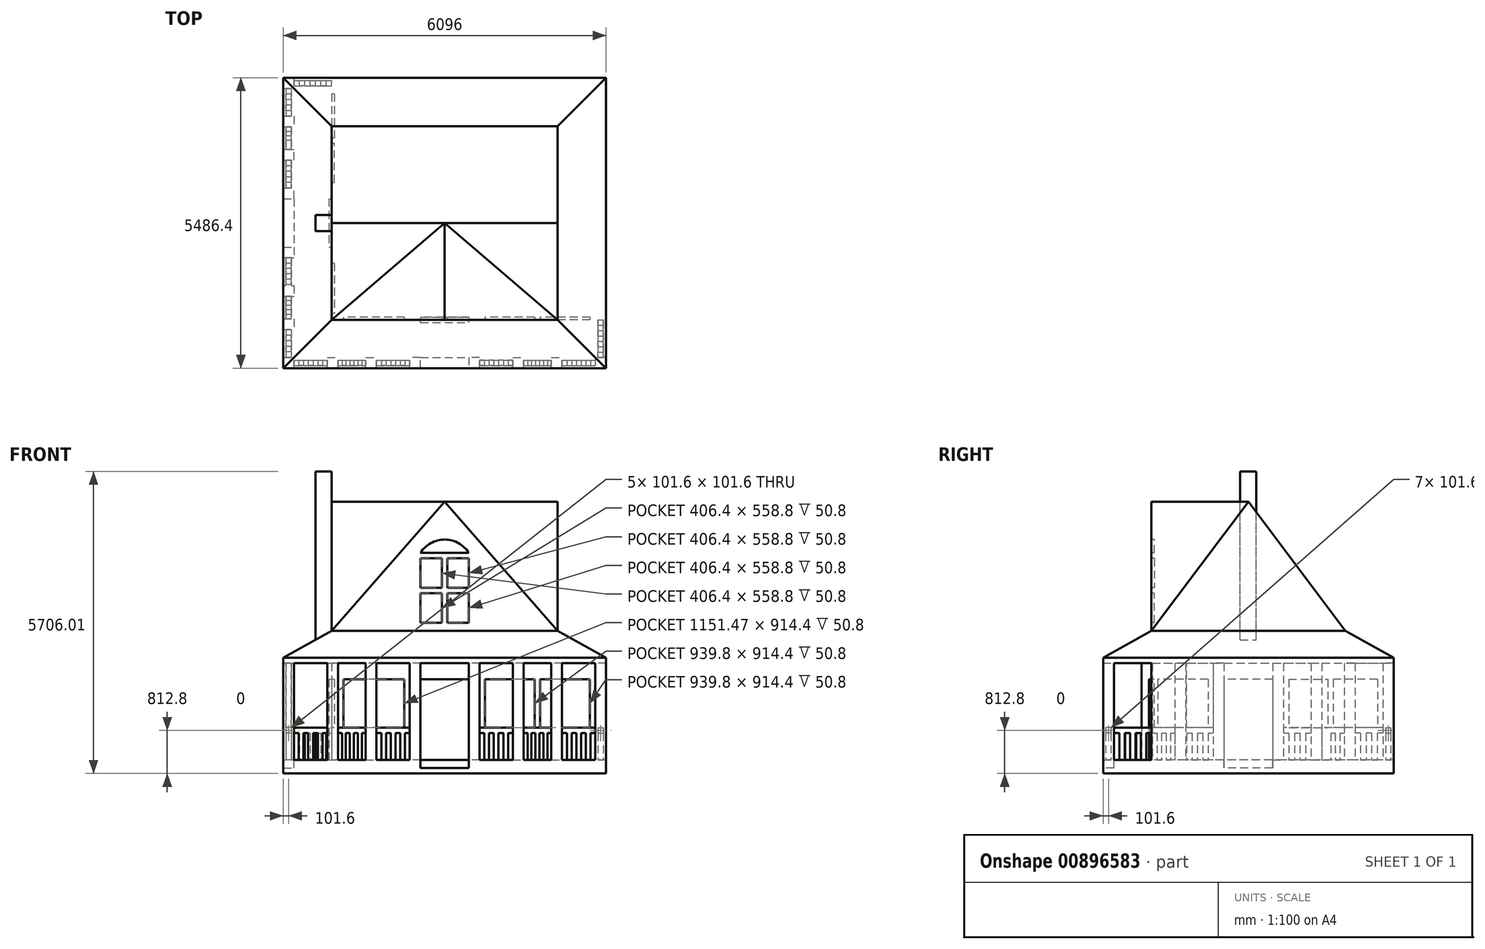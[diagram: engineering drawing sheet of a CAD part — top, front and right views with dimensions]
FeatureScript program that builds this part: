
annotation { "Feature Type Name" : "Feature", "Feature Type Description" : "" }
export const myFeature = defineFeature(function(context is Context, id is Id, definition is map)
    precondition{}
    {
        {
            var Q0;
            Q0=qCreatedBy(makeId("Top.planeOp"),FACE);
            var sketch = newSketch(context, id + "F0", { "sketchPlane" : qUnion([Q0])});
            skLineSegment(sketch, "E0.bottom", {"start": v(-3048, 2743.2) * mm, "end": v(3048, 2743.2) * mm});
            skLineSegment(sketch, "E0.top", {"start": v(-3048, -2743.2) * mm, "end": v(3048, -2743.2) * mm});
            skLineSegment(sketch, "E0.left", {"start": v(-3048, 2743.2) * mm, "end": v(-3048, -2743.2) * mm});
            skLineSegment(sketch, "E0.right", {"start": v(3048, 2743.2) * mm, "end": v(3048, -2743.2) * mm});
            skSolve(sketch);
        }
        {
            var Q0;
            Q0 = qSketchRegion(id + "F0", true);
            extrude(context, id + "F1", {"entities" : qUnion([Q0]), "depth" : 254 * mm, "offsetDistance" : 25.4 * mm});
        }
        {
            var Q0;
            Q0=makeQuery(id+"F1.opExtrude","CAP_FACE",FACE,{"disambiguationData":[OSD([sQuery(id+"F0.wireOp",EDGE,"E0.bottom"),sQuery(id+"F0.wireOp",EDGE,"E0.top"),sQuery(id+"F0.wireOp",EDGE,"E0.left"),sQuery(id+"F0.wireOp",EDGE,"E0.right")])],"isStart":false});
            var sketch = newSketch(context, id + "F2", { "sketchPlane" : qUnion([Q0])});
            skLineSegment(sketch, "E1", {"start": v(-2133.6, 2743.2) * mm, "end": v(-2133.6, -1828.8) * mm, "construction": true});
            skLineSegment(sketch, "E2", {"start": v(-2133.6, -1828.8) * mm, "end": v(3048, -1828.8) * mm, "construction": true});
            skLineSegment(sketch, "E3", {"start": v(0, -2743.2) * mm, "end": v(457.2, -2743.2) * mm, "construction": true});
            skLineSegment(sketch, "E4", {"start": v(0, -2743.2) * mm, "end": v(-457.2, -2743.2) * mm, "construction": true});
            skLineSegment(sketch, "E5", {"start": v(-3048, 0) * mm, "end": v(-3048, 457.2) * mm, "construction": true});
            skLineSegment(sketch, "E6", {"start": v(-3048, 0) * mm, "end": v(-3048, -457.2) * mm, "construction": true});
            skLineSegment(sketch, "E7", {"start": v(3048, -2743.2) * mm, "end": v(3048, -2540) * mm});
            skLineSegment(sketch, "E8", {"start": v(3048, -2540) * mm, "end": v(2844.8, -2540) * mm});
            skLineSegment(sketch, "E9", {"start": v(2844.8, -2540) * mm, "end": v(2844.8, -2743.2) * mm});
            skLineSegment(sketch, "E10", {"start": v(2844.8, -2743.2) * mm, "end": v(3048, -2743.2) * mm});
            skLineSegment(sketch, "E11", {"start": v(457.2, -2743.2) * mm, "end": v(660.4, -2743.2) * mm});
            skLineSegment(sketch, "E12", {"start": v(660.4, -2743.2) * mm, "end": v(660.4, -2540) * mm});
            skLineSegment(sketch, "E13", {"start": v(660.4, -2540) * mm, "end": v(457.2, -2540) * mm});
            skLineSegment(sketch, "E14", {"start": v(457.2, -2540) * mm, "end": v(457.2, -2743.2) * mm});
            skLineSegment(sketch, "E15", {"start": v(660.4, -2641.6) * mm, "end": v(1388.53, -2641.6) * mm, "construction": true});
            skLineSegment(sketch, "E16", {"start": v(1388.53, -2641.6) * mm, "end": v(2116.67, -2641.6) * mm, "construction": true});
            skLineSegment(sketch, "E17", {"start": v(2116.67, -2641.6) * mm, "end": v(2844.8, -2641.6) * mm, "construction": true});
            skLineSegment(sketch, "E18.bottom", {"start": v(1286.93, -2743.2) * mm, "end": v(1490.13, -2743.2) * mm});
            skLineSegment(sketch, "E18.top", {"start": v(1286.93, -2540) * mm, "end": v(1490.13, -2540) * mm});
            skLineSegment(sketch, "E18.left", {"start": v(1286.93, -2743.2) * mm, "end": v(1286.93, -2540) * mm});
            skLineSegment(sketch, "E18.right", {"start": v(1490.13, -2743.2) * mm, "end": v(1490.13, -2540) * mm});
            skLineSegment(sketch, "E19.bottom", {"start": v(2015.07, -2743.2) * mm, "end": v(2218.27, -2743.2) * mm});
            skLineSegment(sketch, "E19.top", {"start": v(2015.07, -2540) * mm, "end": v(2218.27, -2540) * mm});
            skLineSegment(sketch, "E19.left", {"start": v(2015.07, -2743.2) * mm, "end": v(2015.07, -2540) * mm});
            skLineSegment(sketch, "E19.right", {"start": v(2218.27, -2743.2) * mm, "end": v(2218.27, -2540) * mm});
            skLineSegment(sketch, "E20", {"start": v(660.4, -2692.4) * mm, "end": v(1286.93, -2692.4) * mm});
            skLineSegment(sketch, "E21", {"start": v(1490.13, -2692.4) * mm, "end": v(2015.07, -2692.4) * mm});
            skLineSegment(sketch, "E22", {"start": v(2218.27, -2692.4) * mm, "end": v(2844.8, -2692.4) * mm});
            skLineSegment(sketch, "E23", {"start": v(660.4, -2590.8) * mm, "end": v(1286.93, -2590.8) * mm});
            skLineSegment(sketch, "E24", {"start": v(1490.13, -2590.8) * mm, "end": v(2015.07, -2590.8) * mm});
            skLineSegment(sketch, "E25", {"start": v(2218.27, -2590.8) * mm, "end": v(2844.8, -2590.8) * mm});
            skLineSegment(sketch, "E26.bottom", {"start": v(-457.2, -2743.2) * mm, "end": v(-660.4, -2743.2) * mm});
            skLineSegment(sketch, "E26.top", {"start": v(-457.2, -2540) * mm, "end": v(-660.4, -2540) * mm});
            skLineSegment(sketch, "E26.left", {"start": v(-457.2, -2743.2) * mm, "end": v(-457.2, -2540) * mm});
            skLineSegment(sketch, "E26.right", {"start": v(-660.4, -2743.2) * mm, "end": v(-660.4, -2540) * mm});
            skLineSegment(sketch, "E27.bottom", {"start": v(-3048, -2743.2) * mm, "end": v(-2844.8, -2743.2) * mm});
            skLineSegment(sketch, "E27.top", {"start": v(-3048, -2540) * mm, "end": v(-2844.8, -2540) * mm});
            skLineSegment(sketch, "E27.left", {"start": v(-3048, -2743.2) * mm, "end": v(-3048, -2540) * mm});
            skLineSegment(sketch, "E27.right", {"start": v(-2844.8, -2743.2) * mm, "end": v(-2844.8, -2540) * mm});
            skLineSegment(sketch, "E28", {"start": v(-2844.8, -2641.6) * mm, "end": v(-2116.67, -2641.6) * mm, "construction": true});
            skLineSegment(sketch, "E29", {"start": v(-2116.67, -2641.6) * mm, "end": v(-1388.53, -2641.6) * mm, "construction": true});
            skLineSegment(sketch, "E30", {"start": v(-1388.53, -2641.6) * mm, "end": v(-660.4, -2641.6) * mm, "construction": true});
            skLineSegment(sketch, "E31.bottom", {"start": v(-2218.27, -2743.2) * mm, "end": v(-2015.07, -2743.2) * mm});
            skLineSegment(sketch, "E31.top", {"start": v(-2218.27, -2540) * mm, "end": v(-2015.07, -2540) * mm});
            skLineSegment(sketch, "E31.left", {"start": v(-2218.27, -2743.2) * mm, "end": v(-2218.27, -2540) * mm});
            skLineSegment(sketch, "E31.right", {"start": v(-2015.07, -2743.2) * mm, "end": v(-2015.07, -2540) * mm});
            skLineSegment(sketch, "E32.bottom", {"start": v(-1490.13, -2743.2) * mm, "end": v(-1286.93, -2743.2) * mm});
            skLineSegment(sketch, "E32.top", {"start": v(-1490.13, -2540) * mm, "end": v(-1286.93, -2540) * mm});
            skLineSegment(sketch, "E32.left", {"start": v(-1490.13, -2743.2) * mm, "end": v(-1490.13, -2540) * mm});
            skLineSegment(sketch, "E32.right", {"start": v(-1286.93, -2743.2) * mm, "end": v(-1286.93, -2540) * mm});
            skLineSegment(sketch, "E33", {"start": v(-457.2, -2692.4) * mm, "end": v(-660.4, -2692.4) * mm, "construction": true});
            skLineSegment(sketch, "E34", {"start": v(-660.4, -2692.4) * mm, "end": v(-1286.93, -2692.4) * mm});
            skLineSegment(sketch, "E35", {"start": v(-1286.93, -2692.4) * mm, "end": v(-1490.13, -2692.4) * mm, "construction": true});
            skLineSegment(sketch, "E36", {"start": v(-1490.13, -2692.4) * mm, "end": v(-2015.07, -2692.4) * mm});
            skLineSegment(sketch, "E37", {"start": v(-2015.07, -2692.4) * mm, "end": v(-2218.27, -2692.4) * mm, "construction": true});
            skLineSegment(sketch, "E38", {"start": v(-2218.27, -2692.4) * mm, "end": v(-2844.8, -2692.4) * mm});
            skLineSegment(sketch, "E39", {"start": v(-2844.8, -2590.8) * mm, "end": v(-2218.27, -2590.8) * mm});
            skLineSegment(sketch, "E40", {"start": v(-2218.27, -2590.8) * mm, "end": v(-2015.07, -2590.8) * mm, "construction": true});
            skLineSegment(sketch, "E41", {"start": v(-2015.07, -2590.8) * mm, "end": v(-1490.13, -2590.8) * mm});
            skLineSegment(sketch, "E42", {"start": v(-1490.13, -2590.8) * mm, "end": v(-1286.93, -2590.8) * mm, "construction": true});
            skLineSegment(sketch, "E43", {"start": v(-1286.93, -2590.8) * mm, "end": v(-660.4, -2590.8) * mm});
            skLineSegment(sketch, "E44", {"start": v(-660.4, -2590.8) * mm, "end": v(-457.2, -2590.8) * mm, "construction": true});
            skLineSegment(sketch, "E45", {"start": v(-3048, -457.2) * mm, "end": v(-2844.8, -457.2) * mm});
            skLineSegment(sketch, "E46", {"start": v(-2844.8, -457.2) * mm, "end": v(-2844.8, -660.4) * mm});
            skLineSegment(sketch, "E47", {"start": v(-2844.8, -660.4) * mm, "end": v(-3048, -660.4) * mm});
            skLineSegment(sketch, "E48", {"start": v(-3048, -660.4) * mm, "end": v(-3048, -457.2) * mm});
            skLineSegment(sketch, "E49", {"start": v(-2946.4, -660.4) * mm, "end": v(-2946.4, -1286.93) * mm, "construction": true});
            skLineSegment(sketch, "E50", {"start": v(-2946.4, -1286.93) * mm, "end": v(-2946.4, -1913.47) * mm, "construction": true});
            skLineSegment(sketch, "E51", {"start": v(-2946.4, -1913.47) * mm, "end": v(-2946.4, -2540) * mm, "construction": true});
            skLineSegment(sketch, "E52.bottom", {"start": v(-3048, -1185.33) * mm, "end": v(-2844.8, -1185.33) * mm});
            skLineSegment(sketch, "E52.top", {"start": v(-3048, -1388.53) * mm, "end": v(-2844.8, -1388.53) * mm});
            skLineSegment(sketch, "E52.left", {"start": v(-3048, -1185.33) * mm, "end": v(-3048, -1388.53) * mm});
            skLineSegment(sketch, "E52.right", {"start": v(-2844.8, -1185.33) * mm, "end": v(-2844.8, -1388.53) * mm});
            skLineSegment(sketch, "E53.bottom", {"start": v(-3048, -1811.87) * mm, "end": v(-2844.8, -1811.87) * mm});
            skLineSegment(sketch, "E53.top", {"start": v(-3048, -2015.07) * mm, "end": v(-2844.8, -2015.07) * mm});
            skLineSegment(sketch, "E53.left", {"start": v(-3048, -1811.87) * mm, "end": v(-3048, -2015.07) * mm});
            skLineSegment(sketch, "E53.right", {"start": v(-2844.8, -1811.87) * mm, "end": v(-2844.8, -2015.07) * mm});
            skLineSegment(sketch, "E54.bottom", {"start": v(-3048, 457.2) * mm, "end": v(-2844.8, 457.2) * mm});
            skLineSegment(sketch, "E54.top", {"start": v(-3048, 660.4) * mm, "end": v(-2844.8, 660.4) * mm});
            skLineSegment(sketch, "E54.left", {"start": v(-3048, 457.2) * mm, "end": v(-3048, 660.4) * mm});
            skLineSegment(sketch, "E54.right", {"start": v(-2844.8, 457.2) * mm, "end": v(-2844.8, 660.4) * mm});
            skLineSegment(sketch, "E55.bottom", {"start": v(-3048, 2743.2) * mm, "end": v(-2844.8, 2743.2) * mm});
            skLineSegment(sketch, "E55.top", {"start": v(-3048, 2540) * mm, "end": v(-2844.8, 2540) * mm});
            skLineSegment(sketch, "E55.left", {"start": v(-3048, 2743.2) * mm, "end": v(-3048, 2540) * mm});
            skLineSegment(sketch, "E55.right", {"start": v(-2844.8, 2743.2) * mm, "end": v(-2844.8, 2540) * mm});
            skLineSegment(sketch, "E56", {"start": v(-2946.4, 2540) * mm, "end": v(-2946.4, 1913.47) * mm, "construction": true});
            skLineSegment(sketch, "E57", {"start": v(-2946.4, 1913.47) * mm, "end": v(-2946.4, 1286.93) * mm, "construction": true});
            skLineSegment(sketch, "E58", {"start": v(-2946.4, 1286.93) * mm, "end": v(-2946.4, 660.4) * mm, "construction": true});
            skLineSegment(sketch, "E59", {"start": v(2997.2, -2540) * mm, "end": v(2997.2, -1828.8) * mm});
            skLineSegment(sketch, "E60", {"start": v(2997.2, -1828.8) * mm, "end": v(2895.6, -1828.8) * mm});
            skLineSegment(sketch, "E61", {"start": v(2895.6, -1828.8) * mm, "end": v(2895.6, -2540) * mm});
            skLineSegment(sketch, "E62", {"start": v(-2844.8, 2692.4) * mm, "end": v(-2133.6, 2692.4) * mm});
            skLineSegment(sketch, "E63", {"start": v(-2133.6, 2692.4) * mm, "end": v(-2133.6, 2590.8) * mm});
            skLineSegment(sketch, "E64", {"start": v(-2133.6, 2590.8) * mm, "end": v(-2844.8, 2590.8) * mm});
            skLineSegment(sketch, "E65.bottom", {"start": v(-3048, 2015.07) * mm, "end": v(-2844.8, 2015.07) * mm});
            skLineSegment(sketch, "E65.top", {"start": v(-3048, 1811.87) * mm, "end": v(-2844.8, 1811.87) * mm});
            skLineSegment(sketch, "E65.left", {"start": v(-3048, 2015.07) * mm, "end": v(-3048, 1811.87) * mm});
            skLineSegment(sketch, "E65.right", {"start": v(-2844.8, 2015.07) * mm, "end": v(-2844.8, 1811.87) * mm});
            skLineSegment(sketch, "E66.bottom", {"start": v(-3048, 1185.33) * mm, "end": v(-2844.8, 1185.33) * mm});
            skLineSegment(sketch, "E66.top", {"start": v(-3048, 1388.53) * mm, "end": v(-2844.8, 1388.53) * mm});
            skLineSegment(sketch, "E66.left", {"start": v(-3048, 1185.33) * mm, "end": v(-3048, 1388.53) * mm});
            skLineSegment(sketch, "E66.right", {"start": v(-2844.8, 1185.33) * mm, "end": v(-2844.8, 1388.53) * mm});
            skLineSegment(sketch, "E67", {"start": v(-2997.2, -2540) * mm, "end": v(-2997.2, -2015.07) * mm});
            skLineSegment(sketch, "E68", {"start": v(-2895.6, -2540) * mm, "end": v(-2895.6, -2015.07) * mm});
            skLineSegment(sketch, "E69", {"start": v(-2997.2, -2015.07) * mm, "end": v(-2997.2, -1811.87) * mm, "construction": true});
            skLineSegment(sketch, "E70", {"start": v(-2997.2, -1811.87) * mm, "end": v(-2997.2, -1388.53) * mm});
            skLineSegment(sketch, "E71", {"start": v(-2997.2, -1388.53) * mm, "end": v(-2997.2, -1185.33) * mm, "construction": true});
            skLineSegment(sketch, "E72", {"start": v(-2997.2, -1185.33) * mm, "end": v(-2997.2, -660.4) * mm});
            skLineSegment(sketch, "E73", {"start": v(-2895.6, -2015.07) * mm, "end": v(-2895.6, -1811.87) * mm, "construction": true});
            skLineSegment(sketch, "E74", {"start": v(-2895.6, -1811.87) * mm, "end": v(-2895.6, -1388.53) * mm});
            skLineSegment(sketch, "E75", {"start": v(-2895.6, -1388.53) * mm, "end": v(-2895.6, -1185.33) * mm, "construction": true});
            skLineSegment(sketch, "E76", {"start": v(-2895.6, -1185.33) * mm, "end": v(-2895.6, -660.4) * mm});
            skLineSegment(sketch, "E77", {"start": v(-2997.2, 660.4) * mm, "end": v(-2997.2, 1185.33) * mm});
            skLineSegment(sketch, "E78", {"start": v(-2895.6, 660.4) * mm, "end": v(-2895.6, 1185.33) * mm});
            skLineSegment(sketch, "E79", {"start": v(-2997.2, 1185.33) * mm, "end": v(-2997.2, 1388.53) * mm, "construction": true});
            skLineSegment(sketch, "E80", {"start": v(-2997.2, 1388.53) * mm, "end": v(-2997.2, 1811.87) * mm});
            skLineSegment(sketch, "E81", {"start": v(-2997.2, 1811.87) * mm, "end": v(-2997.2, 2015.07) * mm, "construction": true});
            skLineSegment(sketch, "E82", {"start": v(-2997.2, 2015.07) * mm, "end": v(-2997.2, 2540) * mm});
            skLineSegment(sketch, "E83", {"start": v(-2895.6, 1185.33) * mm, "end": v(-2895.6, 1388.53) * mm, "construction": true});
            skLineSegment(sketch, "E84", {"start": v(-2895.6, 1388.53) * mm, "end": v(-2895.6, 1811.87) * mm});
            skLineSegment(sketch, "E85", {"start": v(-2895.6, 1811.87) * mm, "end": v(-2895.6, 2015.07) * mm, "construction": true});
            skLineSegment(sketch, "E86", {"start": v(-2895.6, 2015.07) * mm, "end": v(-2895.6, 2540) * mm});
            skSolve(sketch);
        }
        {
            var Q0;
            Q0 = qSketchRegion(id + "F2", true);
            extrude(context, id + "F3", {"entities" : qUnion([Q0]), "operationType" : NewBodyOperationType.ADD, "depth" : 1828.8 * mm, "offsetDistance" : 25.4 * mm});
        }
        {
            var Q0;
            Q0=makeQuery(id+"F3.opExtrude","SWEPT_FACE",FACE,{"disambiguationData":[OSD([sQuery(id+"F2.wireOp",EDGE,"E22")])]});
            var sketch = newSketch(context, id + "F4", { "sketchPlane" : qUnion([Q0])});
            skLineSegment(sketch, "E87.0", {"start": v(-2844.8, 863.6) * mm, "end": v(-2218.27, 863.6) * mm});
            skLineSegment(sketch, "E88", {"start": v(2844.8, 863.6) * mm, "end": v(2844.8, 2082.8) * mm});
            skLineSegment(sketch, "E89", {"start": v(2844.8, 2082.8) * mm, "end": v(2218.27, 2082.8) * mm});
            skLineSegment(sketch, "E90", {"start": v(2218.27, 2082.8) * mm, "end": v(2218.27, 863.6) * mm});
            skLineSegment(sketch, "E91.1", {"start": v(1490.13, 2082.8) * mm, "end": v(1490.13, 863.6) * mm});
            skLineSegment(sketch, "E91.2", {"start": v(2015.07, 2082.8) * mm, "end": v(1490.13, 2082.8) * mm});
            skLineSegment(sketch, "E91.3", {"start": v(2015.07, 863.6) * mm, "end": v(2015.07, 2082.8) * mm});
            skLineSegment(sketch, "E92.1", {"start": v(660.4, 2082.8) * mm, "end": v(660.4, 863.6) * mm});
            skLineSegment(sketch, "E92.2", {"start": v(1286.93, 2082.8) * mm, "end": v(660.4, 2082.8) * mm});
            skLineSegment(sketch, "E92.3", {"start": v(1286.93, 863.6) * mm, "end": v(1286.93, 2082.8) * mm});
            skLineSegment(sketch, "E93.1", {"start": v(-1286.93, 2082.8) * mm, "end": v(-1286.93, 863.6) * mm});
            skLineSegment(sketch, "E93.2", {"start": v(-660.4, 2082.8) * mm, "end": v(-1286.93, 2082.8) * mm});
            skLineSegment(sketch, "E93.3", {"start": v(-660.4, 863.6) * mm, "end": v(-660.4, 2082.8) * mm});
            skLineSegment(sketch, "E94.1", {"start": v(-2015.07, 2082.8) * mm, "end": v(-2015.07, 863.6) * mm});
            skLineSegment(sketch, "E94.2", {"start": v(-1490.13, 2082.8) * mm, "end": v(-2015.07, 2082.8) * mm});
            skLineSegment(sketch, "E94.3", {"start": v(-1490.13, 863.6) * mm, "end": v(-1490.13, 2082.8) * mm});
            skLineSegment(sketch, "E95.1", {"start": v(-2844.8, 2082.8) * mm, "end": v(-2844.8, 863.6) * mm});
            skLineSegment(sketch, "E95.2", {"start": v(-2218.27, 2082.8) * mm, "end": v(-2844.8, 2082.8) * mm});
            skLineSegment(sketch, "E95.3", {"start": v(-2218.27, 863.6) * mm, "end": v(-2218.27, 2082.8) * mm});
            skLineSegment(sketch, "E96.trimOffspring", {"start": v(2218.27, 863.6) * mm, "end": v(2844.8, 863.6) * mm});
            skLineSegment(sketch, "E97.trimOffspring", {"start": v(1490.13, 863.6) * mm, "end": v(2015.07, 863.6) * mm});
            skLineSegment(sketch, "E98.trimOffspring", {"start": v(660.4, 863.6) * mm, "end": v(1286.93, 863.6) * mm});
            skLineSegment(sketch, "E99.trimOffspring", {"start": v(-1286.93, 863.6) * mm, "end": v(-660.4, 863.6) * mm});
            skLineSegment(sketch, "E100.trimOffspring", {"start": v(-2015.07, 863.6) * mm, "end": v(-1490.13, 863.6) * mm});
            skLineSegment(sketch, "E101.0", {"start": v(2218.27, 762) * mm, "end": v(2307.77, 762) * mm});
            skLineSegment(sketch, "E102.0", {"start": v(1490.13, 762) * mm, "end": v(1565.12, 762) * mm});
            skLineSegment(sketch, "E103.0", {"start": v(-1286.93, 762) * mm, "end": v(-1197.43, 762) * mm});
            skLineSegment(sketch, "E104.0", {"start": v(-2015.07, 762) * mm, "end": v(-1940.08, 762) * mm});
            skLineSegment(sketch, "E105.0", {"start": v(-2844.8, 762) * mm, "end": v(-2755.3, 762) * mm});
            skLineSegment(sketch, "E106", {"start": v(-2665.8, 762) * mm, "end": v(-2576.29, 762) * mm});
            skLineSegment(sketch, "E107", {"start": v(-2486.78, 762) * mm, "end": v(-2397.28, 762) * mm});
            skLineSegment(sketch, "E108", {"start": v(-2307.77, 762) * mm, "end": v(-2218.27, 762) * mm});
            skLineSegment(sketch, "E109.0", {"start": v(-2844.8, 254) * mm, "end": v(-2755.3, 254) * mm});
            skLineSegment(sketch, "E110.0", {"start": v(-2015.07, 254) * mm, "end": v(-1490.13, 254) * mm});
            skLineSegment(sketch, "E111.0", {"start": v(-1286.93, 254) * mm, "end": v(-660.4, 254) * mm});
            skLineSegment(sketch, "E112.0", {"start": v(660.4, 254) * mm, "end": v(1286.93, 254) * mm});
            skLineSegment(sketch, "E113.0", {"start": v(1490.13, 254) * mm, "end": v(2015.07, 254) * mm});
            skLineSegment(sketch, "E114.0", {"start": v(2218.27, 254) * mm, "end": v(2844.8, 254) * mm});
            skLineSegment(sketch, "E115", {"start": v(-2755.3, 762) * mm, "end": v(-2755.3, 254) * mm});
            skLineSegment(sketch, "E116", {"start": v(-2665.8, 762) * mm, "end": v(-2665.8, 254) * mm});
            skLineSegment(sketch, "E117", {"start": v(-2576.29, 762) * mm, "end": v(-2576.29, 254) * mm});
            skLineSegment(sketch, "E118", {"start": v(-2486.78, 762) * mm, "end": v(-2486.78, 254) * mm});
            skLineSegment(sketch, "E119", {"start": v(-2397.28, 762) * mm, "end": v(-2397.28, 254) * mm});
            skLineSegment(sketch, "E120", {"start": v(-2307.77, 762) * mm, "end": v(-2307.77, 254) * mm});
            skLineSegment(sketch, "E121.trimOffspring", {"start": v(-2307.77, 254) * mm, "end": v(-2218.27, 254) * mm});
            skLineSegment(sketch, "E122.trimOffspring", {"start": v(-2486.78, 254) * mm, "end": v(-2397.28, 254) * mm});
            skLineSegment(sketch, "E123.trimOffspring", {"start": v(-2665.8, 254) * mm, "end": v(-2576.29, 254) * mm});
            skLineSegment(sketch, "E124", {"start": v(-2844.8, 762) * mm, "end": v(-2844.8, 254) * mm});
            skLineSegment(sketch, "E125", {"start": v(-2755.3, 254) * mm, "end": v(-2844.8, 254) * mm});
            skLineSegment(sketch, "E126", {"start": v(-2218.27, 762) * mm, "end": v(-2218.27, 254) * mm});
            skLineSegment(sketch, "E127", {"start": v(-1865.09, 762) * mm, "end": v(-1790.1, 762) * mm});
            skLineSegment(sketch, "E128", {"start": v(-1715.1, 762) * mm, "end": v(-1640.11, 762) * mm});
            skLineSegment(sketch, "E129", {"start": v(-1565.12, 762) * mm, "end": v(-1490.13, 762) * mm});
            skLineSegment(sketch, "E130", {"start": v(-1107.92, 762) * mm, "end": v(-1018.42, 762) * mm});
            skLineSegment(sketch, "E131", {"start": v(-928.91, 762) * mm, "end": v(-839.4, 762) * mm});
            skLineSegment(sketch, "E132", {"start": v(-749.9, 762) * mm, "end": v(-660.4, 762) * mm});
            skLineSegment(sketch, "E133", {"start": v(1640.11, 762) * mm, "end": v(1715.1, 762) * mm});
            skLineSegment(sketch, "E134", {"start": v(1790.1, 762) * mm, "end": v(1865.09, 762) * mm});
            skLineSegment(sketch, "E135", {"start": v(1940.08, 762) * mm, "end": v(2015.07, 762) * mm});
            skLineSegment(sketch, "E136", {"start": v(2397.28, 762) * mm, "end": v(2486.78, 762) * mm});
            skLineSegment(sketch, "E137", {"start": v(2576.29, 762) * mm, "end": v(2665.8, 762) * mm});
            skLineSegment(sketch, "E138", {"start": v(2755.3, 762) * mm, "end": v(2844.8, 762) * mm});
            skLineSegment(sketch, "E139", {"start": v(1286.93, 863.6) * mm, "end": v(1286.93, 762) * mm, "construction": true});
            skLineSegment(sketch, "E140", {"start": v(1286.93, 762) * mm, "end": v(1197.43, 762) * mm});
            skLineSegment(sketch, "E141", {"start": v(1107.92, 762) * mm, "end": v(1018.42, 762) * mm});
            skLineSegment(sketch, "E142", {"start": v(928.91, 762) * mm, "end": v(839.4, 762) * mm});
            skLineSegment(sketch, "E143", {"start": v(749.9, 762) * mm, "end": v(660.4, 762) * mm});
            skLineSegment(sketch, "E144", {"start": v(2844.8, 762) * mm, "end": v(2844.8, 254) * mm});
            skLineSegment(sketch, "E145", {"start": v(2755.3, 762) * mm, "end": v(2755.3, 254) * mm});
            skLineSegment(sketch, "E146", {"start": v(2755.3, 254) * mm, "end": v(2844.8, 254) * mm});
            skLineSegment(sketch, "E147", {"start": v(2665.8, 762) * mm, "end": v(2665.8, 254) * mm});
            skLineSegment(sketch, "E148", {"start": v(2576.29, 762) * mm, "end": v(2576.29, 254) * mm});
            skLineSegment(sketch, "E149", {"start": v(2576.29, 254) * mm, "end": v(2665.8, 254) * mm});
            skLineSegment(sketch, "E150", {"start": v(2486.78, 762) * mm, "end": v(2486.78, 254) * mm});
            skLineSegment(sketch, "E151", {"start": v(2397.28, 762) * mm, "end": v(2397.28, 254) * mm});
            skLineSegment(sketch, "E152", {"start": v(2397.28, 254) * mm, "end": v(2486.78, 254) * mm});
            skLineSegment(sketch, "E153", {"start": v(2307.77, 762) * mm, "end": v(2307.77, 254) * mm});
            skLineSegment(sketch, "E154", {"start": v(2307.77, 254) * mm, "end": v(2218.27, 254) * mm});
            skLineSegment(sketch, "E155", {"start": v(2218.27, 762) * mm, "end": v(2218.27, 254) * mm});
            skLineSegment(sketch, "E156.top", {"start": v(1940.08, 254) * mm, "end": v(2015.07, 254) * mm});
            skLineSegment(sketch, "E156.left", {"start": v(1940.08, 762) * mm, "end": v(1940.08, 254) * mm});
            skLineSegment(sketch, "E156.right", {"start": v(2015.07, 762) * mm, "end": v(2015.07, 254) * mm});
            skLineSegment(sketch, "E157", {"start": v(1865.09, 762) * mm, "end": v(1865.09, 254) * mm});
            skLineSegment(sketch, "E158", {"start": v(1790.1, 762) * mm, "end": v(1790.1, 254) * mm});
            skLineSegment(sketch, "E159", {"start": v(1790.1, 254) * mm, "end": v(1865.09, 254) * mm});
            skLineSegment(sketch, "E160", {"start": v(1715.1, 762) * mm, "end": v(1715.1, 254) * mm});
            skLineSegment(sketch, "E161", {"start": v(1640.11, 762) * mm, "end": v(1640.11, 254) * mm});
            skLineSegment(sketch, "E162", {"start": v(1640.11, 254) * mm, "end": v(1715.1, 254) * mm});
            skLineSegment(sketch, "E163", {"start": v(1565.12, 762) * mm, "end": v(1565.12, 254) * mm});
            skLineSegment(sketch, "E164", {"start": v(1565.12, 254) * mm, "end": v(1490.13, 254) * mm});
            skLineSegment(sketch, "E165", {"start": v(1490.13, 762) * mm, "end": v(1490.13, 254) * mm});
            skLineSegment(sketch, "E166", {"start": v(1197.43, 762) * mm, "end": v(1197.43, 254) * mm});
            skLineSegment(sketch, "E167", {"start": v(1286.93, 762) * mm, "end": v(1286.93, 254) * mm});
            skLineSegment(sketch, "E168", {"start": v(1197.43, 254) * mm, "end": v(1286.93, 254) * mm});
            skLineSegment(sketch, "E169", {"start": v(1107.92, 762) * mm, "end": v(1107.92, 254) * mm});
            skLineSegment(sketch, "E170", {"start": v(1018.42, 762) * mm, "end": v(1018.42, 254) * mm});
            skLineSegment(sketch, "E171", {"start": v(1018.42, 254) * mm, "end": v(1107.92, 254) * mm});
            skLineSegment(sketch, "E172", {"start": v(928.91, 762) * mm, "end": v(928.91, 254) * mm});
            skLineSegment(sketch, "E173", {"start": v(839.4, 762) * mm, "end": v(839.4, 254) * mm});
            skLineSegment(sketch, "E174", {"start": v(839.4, 254) * mm, "end": v(928.91, 254) * mm});
            skLineSegment(sketch, "E175", {"start": v(749.9, 762) * mm, "end": v(749.9, 254) * mm});
            skLineSegment(sketch, "E176", {"start": v(749.9, 254) * mm, "end": v(660.4, 254) * mm});
            skLineSegment(sketch, "E177", {"start": v(660.4, 762) * mm, "end": v(660.4, 254) * mm});
            skLineSegment(sketch, "E178.bottom", {"start": v(-1197.43, 762) * mm, "end": v(-1286.93, 762) * mm});
            skLineSegment(sketch, "E178.top", {"start": v(-1197.43, 254) * mm, "end": v(-1286.93, 254) * mm});
            skLineSegment(sketch, "E178.left", {"start": v(-1197.43, 762) * mm, "end": v(-1197.43, 254) * mm});
            skLineSegment(sketch, "E178.right", {"start": v(-1286.93, 762) * mm, "end": v(-1286.93, 254) * mm});
            skLineSegment(sketch, "E179.top", {"start": v(-749.9, 254) * mm, "end": v(-660.4, 254) * mm});
            skLineSegment(sketch, "E179.left", {"start": v(-749.9, 762) * mm, "end": v(-749.9, 254) * mm});
            skLineSegment(sketch, "E179.right", {"start": v(-660.4, 762) * mm, "end": v(-660.4, 254) * mm});
            skLineSegment(sketch, "E180.bottom", {"start": v(-1940.08, 762) * mm, "end": v(-2015.07, 762) * mm});
            skLineSegment(sketch, "E180.top", {"start": v(-1940.08, 254) * mm, "end": v(-2015.07, 254) * mm});
            skLineSegment(sketch, "E180.left", {"start": v(-1940.08, 762) * mm, "end": v(-1940.08, 254) * mm});
            skLineSegment(sketch, "E180.right", {"start": v(-2015.07, 762) * mm, "end": v(-2015.07, 254) * mm});
            skLineSegment(sketch, "E181.top", {"start": v(-1565.12, 254) * mm, "end": v(-1490.13, 254) * mm});
            skLineSegment(sketch, "E181.left", {"start": v(-1565.12, 762) * mm, "end": v(-1565.12, 254) * mm});
            skLineSegment(sketch, "E181.right", {"start": v(-1490.13, 762) * mm, "end": v(-1490.13, 254) * mm});
            skLineSegment(sketch, "E182", {"start": v(-1865.09, 762) * mm, "end": v(-1865.09, 254) * mm});
            skLineSegment(sketch, "E183", {"start": v(-1790.1, 762) * mm, "end": v(-1790.1, 254) * mm});
            skLineSegment(sketch, "E184", {"start": v(-1715.1, 762) * mm, "end": v(-1715.1, 254) * mm});
            skLineSegment(sketch, "E185", {"start": v(-1640.11, 762) * mm, "end": v(-1640.11, 254) * mm});
            skLineSegment(sketch, "E186", {"start": v(-1640.11, 254) * mm, "end": v(-1715.1, 254) * mm});
            skLineSegment(sketch, "E187", {"start": v(-1790.1, 254) * mm, "end": v(-1865.09, 254) * mm});
            skLineSegment(sketch, "E188", {"start": v(-1107.92, 762) * mm, "end": v(-1107.92, 254) * mm});
            skLineSegment(sketch, "E189", {"start": v(-1018.42, 762) * mm, "end": v(-1018.42, 254) * mm});
            skLineSegment(sketch, "E190", {"start": v(-928.91, 762) * mm, "end": v(-928.91, 254) * mm});
            skLineSegment(sketch, "E191", {"start": v(-839.4, 762) * mm, "end": v(-839.4, 254) * mm});
            skLineSegment(sketch, "E192", {"start": v(-839.4, 254) * mm, "end": v(-928.91, 254) * mm});
            skLineSegment(sketch, "E193", {"start": v(-1018.42, 254) * mm, "end": v(-1107.92, 254) * mm});
            skSolve(sketch);
        }
        {
            var Q0;
            Q0 = qSketchRegion(id + "F4", true);
            extrude(context, id + "F5", {"entities" : qUnion([Q0]), "operationType" : NewBodyOperationType.REMOVE, "oppositeDirection" : true, "depth" : 101.6 * mm, "offsetDistance" : 25.4 * mm});
        }
        {
            var Q0;
            Q0=makeQuery(id+"F3.opExtrude","SWEPT_FACE",FACE,{"disambiguationData":[OSD([sQuery(id+"F2.wireOp",EDGE,"E67")])]});
            var sketch = newSketch(context, id + "F6", { "sketchPlane" : qUnion([Q0])});
            skLineSegment(sketch, "E194.0", {"start": v(2015.07, 863.6) * mm, "end": v(2540, 863.6) * mm});
            skLineSegment(sketch, "E195.0", {"start": v(1388.53, 863.6) * mm, "end": v(1811.87, 863.6) * mm});
            skLineSegment(sketch, "E196.0", {"start": v(654.9, 863.6) * mm, "end": v(1163.3, 863.6) * mm});
            skLineSegment(sketch, "E197.0", {"start": v(-1185.33, 863.6) * mm, "end": v(-660.4, 863.6) * mm});
            skLineSegment(sketch, "E198.0", {"start": v(-1811.87, 863.6) * mm, "end": v(-1388.53, 863.6) * mm});
            skLineSegment(sketch, "E199.0", {"start": v(-2540, 863.6) * mm, "end": v(-2015.07, 863.6) * mm});
            skLineSegment(sketch, "E200", {"start": v(-2540, 863.6) * mm, "end": v(-2540, 2082.8) * mm});
            skLineSegment(sketch, "E201", {"start": v(-2540, 2082.8) * mm, "end": v(-2015.07, 2082.8) * mm});
            skLineSegment(sketch, "E202", {"start": v(2540, 2082.8) * mm, "end": v(2540, 863.6) * mm});
            skLineSegment(sketch, "E203", {"start": v(2015.07, 863.6) * mm, "end": v(2015.07, 2082.8) * mm});
            skLineSegment(sketch, "E204", {"start": v(1811.87, 863.6) * mm, "end": v(1811.87, 2082.8) * mm});
            skLineSegment(sketch, "E205", {"start": v(1388.53, 863.6) * mm, "end": v(1388.53, 2082.8) * mm});
            skLineSegment(sketch, "E206", {"start": v(1163.3, 863.6) * mm, "end": v(1163.3, 2082.8) * mm});
            skLineSegment(sketch, "E207", {"start": v(654.9, 863.6) * mm, "end": v(654.9, 2082.8) * mm});
            skLineSegment(sketch, "E208", {"start": v(-660.4, 863.6) * mm, "end": v(-660.4, 2082.8) * mm});
            skLineSegment(sketch, "E209", {"start": v(-1185.33, 863.6) * mm, "end": v(-1185.33, 2082.8) * mm});
            skLineSegment(sketch, "E210", {"start": v(-1388.53, 863.6) * mm, "end": v(-1388.53, 2082.8) * mm});
            skLineSegment(sketch, "E211", {"start": v(-1811.87, 863.6) * mm, "end": v(-1811.87, 2082.8) * mm});
            skLineSegment(sketch, "E212", {"start": v(-2015.07, 863.6) * mm, "end": v(-2015.07, 2082.8) * mm});
            skLineSegment(sketch, "E213.trimOffspring", {"start": v(-1811.87, 2082.8) * mm, "end": v(-1388.53, 2082.8) * mm});
            skLineSegment(sketch, "E214.trimOffspring", {"start": v(-1185.33, 2082.8) * mm, "end": v(-660.4, 2082.8) * mm});
            skLineSegment(sketch, "E215.trimOffspring", {"start": v(654.9, 2082.8) * mm, "end": v(1163.3, 2082.8) * mm});
            skLineSegment(sketch, "E216.trimOffspring", {"start": v(1388.53, 2082.8) * mm, "end": v(1811.87, 2082.8) * mm});
            skLineSegment(sketch, "E217", {"start": v(2015.07, 2082.8) * mm, "end": v(2540, 2082.8) * mm});
            skLineSegment(sketch, "E218", {"start": v(2015.07, 762) * mm, "end": v(2120.05, 762) * mm});
            skLineSegment(sketch, "E219", {"start": v(2120.05, 762) * mm, "end": v(2225.04, 762) * mm, "construction": true});
            skLineSegment(sketch, "E220", {"start": v(2225.04, 762) * mm, "end": v(2330.03, 762) * mm});
            skLineSegment(sketch, "E221", {"start": v(2330.03, 762) * mm, "end": v(2435.01, 762) * mm, "construction": true});
            skLineSegment(sketch, "E222", {"start": v(2435.01, 762) * mm, "end": v(2540, 762) * mm});
            skLineSegment(sketch, "E223.bottom", {"start": v(2120.05, 762) * mm, "end": v(2015.07, 762) * mm});
            skLineSegment(sketch, "E223.top", {"start": v(2120.05, 254) * mm, "end": v(2015.07, 254) * mm});
            skLineSegment(sketch, "E223.left", {"start": v(2120.05, 762) * mm, "end": v(2120.05, 254) * mm});
            skLineSegment(sketch, "E223.right", {"start": v(2015.07, 762) * mm, "end": v(2015.07, 254) * mm});
            skLineSegment(sketch, "E224.top", {"start": v(2435.01, 254) * mm, "end": v(2540, 254) * mm});
            skLineSegment(sketch, "E224.left", {"start": v(2435.01, 762) * mm, "end": v(2435.01, 254) * mm});
            skLineSegment(sketch, "E224.right", {"start": v(2540, 762) * mm, "end": v(2540, 254) * mm});
            skLineSegment(sketch, "E225", {"start": v(2330.03, 762) * mm, "end": v(2330.03, 254) * mm});
            skLineSegment(sketch, "E226", {"start": v(2225.04, 762) * mm, "end": v(2225.04, 254) * mm});
            skLineSegment(sketch, "E227", {"start": v(2225.04, 254) * mm, "end": v(2330.03, 254) * mm});
            skLineSegment(sketch, "E228", {"start": v(1811.87, 863.6) * mm, "end": v(1811.87, 762) * mm, "construction": true});
            skLineSegment(sketch, "E229", {"start": v(1811.87, 762) * mm, "end": v(1726.46, 762) * mm});
            skLineSegment(sketch, "E230", {"start": v(1726.46, 762) * mm, "end": v(1641.05, 762) * mm, "construction": true});
            skLineSegment(sketch, "E231", {"start": v(1641.05, 762) * mm, "end": v(1555.65, 762) * mm});
            skLineSegment(sketch, "E232", {"start": v(1555.65, 762) * mm, "end": v(1470.24, 762) * mm, "construction": true});
            skLineSegment(sketch, "E233", {"start": v(1470.24, 762) * mm, "end": v(1384.84, 762) * mm});
            skLineSegment(sketch, "E234", {"start": v(1163.3, 863.6) * mm, "end": v(1163.3, 762) * mm, "construction": true});
            skLineSegment(sketch, "E235", {"start": v(1163.3, 762) * mm, "end": v(1062.72, 762) * mm});
            skLineSegment(sketch, "E236", {"start": v(1062.72, 762) * mm, "end": v(962.14, 762) * mm, "construction": true});
            skLineSegment(sketch, "E237", {"start": v(962.14, 762) * mm, "end": v(861.56, 762) * mm});
            skLineSegment(sketch, "E238", {"start": v(861.56, 762) * mm, "end": v(760.98, 762) * mm, "construction": true});
            skLineSegment(sketch, "E239", {"start": v(760.98, 762) * mm, "end": v(660.4, 762) * mm});
            skLineSegment(sketch, "E240", {"start": v(1811.87, 254) * mm, "end": v(1726.46, 254) * mm});
            skLineSegment(sketch, "E241", {"start": v(1811.87, 762) * mm, "end": v(1811.87, 254) * mm});
            skLineSegment(sketch, "E242", {"start": v(1726.46, 762) * mm, "end": v(1726.46, 254) * mm});
            skLineSegment(sketch, "E243", {"start": v(1470.24, 762) * mm, "end": v(1470.24, 254) * mm});
            skLineSegment(sketch, "E244", {"start": v(1384.84, 762) * mm, "end": v(1384.84, 254) * mm});
            skLineSegment(sketch, "E245", {"start": v(1555.65, 762) * mm, "end": v(1555.65, 254) * mm});
            skLineSegment(sketch, "E246", {"start": v(1641.05, 762) * mm, "end": v(1641.05, 254) * mm});
            skLineSegment(sketch, "E247.trimOffspring", {"start": v(1641.05, 254) * mm, "end": v(1555.65, 254) * mm});
            skLineSegment(sketch, "E248.trimOffspring", {"start": v(1470.24, 254) * mm, "end": v(1384.84, 254) * mm});
            skLineSegment(sketch, "E249", {"start": v(1163.3, 762) * mm, "end": v(1163.3, 254) * mm});
            skLineSegment(sketch, "E250", {"start": v(1062.72, 762) * mm, "end": v(1062.72, 254) * mm});
            skLineSegment(sketch, "E251", {"start": v(962.14, 762) * mm, "end": v(962.14, 254) * mm});
            skLineSegment(sketch, "E252", {"start": v(861.56, 762) * mm, "end": v(861.56, 254) * mm});
            skLineSegment(sketch, "E253", {"start": v(760.98, 762) * mm, "end": v(760.98, 254) * mm});
            skLineSegment(sketch, "E254", {"start": v(660.4, 762) * mm, "end": v(660.4, 254) * mm});
            skLineSegment(sketch, "E255.trimOffspring", {"start": v(1163.3, 254) * mm, "end": v(1062.72, 254) * mm});
            skLineSegment(sketch, "E256.trimOffspring", {"start": v(962.14, 254) * mm, "end": v(861.56, 254) * mm});
            skLineSegment(sketch, "E257.trimOffspring", {"start": v(760.98, 254) * mm, "end": v(660.4, 254) * mm});
            skLineSegment(sketch, "E258", {"start": v(-660.4, 254) * mm, "end": v(-765.39, 254) * mm});
            skLineSegment(sketch, "E259", {"start": v(-660.4, 863.6) * mm, "end": v(-660.4, 762) * mm, "construction": true});
            skLineSegment(sketch, "E260", {"start": v(-660.4, 762) * mm, "end": v(-765.39, 762) * mm});
            skLineSegment(sketch, "E261", {"start": v(-765.39, 762) * mm, "end": v(-870.37, 762) * mm, "construction": true});
            skLineSegment(sketch, "E262", {"start": v(-870.37, 762) * mm, "end": v(-975.36, 762) * mm});
            skLineSegment(sketch, "E263", {"start": v(-975.36, 762) * mm, "end": v(-1080.35, 762) * mm, "construction": true});
            skLineSegment(sketch, "E264", {"start": v(-1080.35, 762) * mm, "end": v(-1185.33, 762) * mm});
            skLineSegment(sketch, "E265", {"start": v(-765.39, 762) * mm, "end": v(-765.39, 254) * mm});
            skLineSegment(sketch, "E266", {"start": v(-660.4, 762) * mm, "end": v(-660.4, 254) * mm});
            skLineSegment(sketch, "E267", {"start": v(-870.37, 762) * mm, "end": v(-870.37, 254) * mm});
            skLineSegment(sketch, "E268", {"start": v(-975.36, 762) * mm, "end": v(-975.36, 254) * mm});
            skLineSegment(sketch, "E269", {"start": v(-1080.35, 762) * mm, "end": v(-1080.35, 254) * mm});
            skLineSegment(sketch, "E270", {"start": v(-1185.33, 762) * mm, "end": v(-1185.33, 254) * mm});
            skLineSegment(sketch, "E271.trimOffspring", {"start": v(-1080.35, 254) * mm, "end": v(-1185.33, 254) * mm});
            skLineSegment(sketch, "E272.trimOffspring", {"start": v(-870.37, 254) * mm, "end": v(-975.36, 254) * mm});
            skLineSegment(sketch, "E273", {"start": v(-1388.53, 863.6) * mm, "end": v(-1388.53, 762) * mm, "construction": true});
            skLineSegment(sketch, "E274", {"start": v(-1388.53, 762) * mm, "end": v(-1473.2, 762) * mm});
            skLineSegment(sketch, "E275", {"start": v(-1473.2, 762) * mm, "end": v(-1557.87, 762) * mm, "construction": true});
            skLineSegment(sketch, "E276", {"start": v(-1557.87, 762) * mm, "end": v(-1642.53, 762) * mm});
            skLineSegment(sketch, "E277", {"start": v(-1642.53, 762) * mm, "end": v(-1727.2, 762) * mm, "construction": true});
            skLineSegment(sketch, "E278", {"start": v(-1811.87, 863.6) * mm, "end": v(-1811.87, 762) * mm, "construction": true});
            skLineSegment(sketch, "E279", {"start": v(-1727.2, 762) * mm, "end": v(-1811.87, 762) * mm});
            skLineSegment(sketch, "E280", {"start": v(-1811.87, 762) * mm, "end": v(-1811.87, 254) * mm});
            skLineSegment(sketch, "E281", {"start": v(-1727.2, 762) * mm, "end": v(-1727.2, 254) * mm});
            skLineSegment(sketch, "E282", {"start": v(-1642.53, 762) * mm, "end": v(-1642.53, 254) * mm});
            skLineSegment(sketch, "E283", {"start": v(-1557.87, 762) * mm, "end": v(-1557.87, 254) * mm});
            skLineSegment(sketch, "E284", {"start": v(-1473.2, 762) * mm, "end": v(-1473.2, 254) * mm});
            skLineSegment(sketch, "E285", {"start": v(-1388.53, 762) * mm, "end": v(-1388.53, 254) * mm});
            skLineSegment(sketch, "E286.trimOffspring", {"start": v(-1557.87, 254) * mm, "end": v(-1811.87, 254) * mm});
            skLineSegment(sketch, "E287", {"start": v(-2015.07, 863.6) * mm, "end": v(-2015.07, 762) * mm, "construction": true});
            skLineSegment(sketch, "E288", {"start": v(-2540, 863.6) * mm, "end": v(-2540, 762) * mm, "construction": true});
            skLineSegment(sketch, "E289", {"start": v(-2540, 762) * mm, "end": v(-2435.01, 762) * mm});
            skLineSegment(sketch, "E290", {"start": v(-2435.01, 762) * mm, "end": v(-2330.03, 762) * mm, "construction": true});
            skLineSegment(sketch, "E291", {"start": v(-2330.03, 762) * mm, "end": v(-2225.04, 762) * mm});
            skLineSegment(sketch, "E292", {"start": v(-2225.04, 762) * mm, "end": v(-2120.05, 762) * mm, "construction": true});
            skLineSegment(sketch, "E293", {"start": v(-2120.05, 762) * mm, "end": v(-2015.07, 762) * mm});
            skLineSegment(sketch, "E294", {"start": v(-2120.05, 762) * mm, "end": v(-2120.05, 254) * mm});
            skLineSegment(sketch, "E295", {"start": v(-2015.07, 762) * mm, "end": v(-2015.07, 254) * mm});
            skLineSegment(sketch, "E296", {"start": v(-2225.04, 762) * mm, "end": v(-2225.04, 254) * mm});
            skLineSegment(sketch, "E297", {"start": v(-2330.03, 762) * mm, "end": v(-2330.03, 254) * mm});
            skLineSegment(sketch, "E298", {"start": v(-2435.01, 762) * mm, "end": v(-2435.01, 254) * mm});
            skLineSegment(sketch, "E299", {"start": v(-2540, 762) * mm, "end": v(-2540, 254) * mm});
            skLineSegment(sketch, "E300.trimOffspring", {"start": v(-2435.01, 254) * mm, "end": v(-2540, 254) * mm});
            skLineSegment(sketch, "E301.trimOffspring", {"start": v(-2225.04, 254) * mm, "end": v(-2330.03, 254) * mm});
            skLineSegment(sketch, "E302.trimOffspring", {"start": v(-2015.07, 254) * mm, "end": v(-2120.05, 254) * mm});
            skSolve(sketch);
        }
        {
            var Q0;
            Q0 = qSketchRegion(id + "F6", true);
            extrude(context, id + "F7", {"entities" : qUnion([Q0]), "operationType" : NewBodyOperationType.REMOVE, "oppositeDirection" : true, "depth" : 101.6 * mm, "offsetDistance" : 25.4 * mm});
        }
        {
            var Q0;
            Q0=makeQuery(id+"F3.opExtrude","SWEPT_FACE",FACE,{"disambiguationData":[OSD([sQuery(id+"F2.wireOp",EDGE,"E62")])]});
            var sketch = newSketch(context, id + "F8", { "sketchPlane" : qUnion([Q0])});
            skLineSegment(sketch, "E303", {"start": v(2844.8, 863.6) * mm, "end": v(2133.6, 863.6) * mm});
            skLineSegment(sketch, "E304", {"start": v(2133.6, 863.6) * mm, "end": v(2133.6, 2082.8) * mm});
            skLineSegment(sketch, "E305", {"start": v(2133.6, 2082.8) * mm, "end": v(2844.8, 2082.8) * mm});
            skLineSegment(sketch, "E306", {"start": v(2844.8, 2082.8) * mm, "end": v(2844.8, 863.6) * mm});
            skLineSegment(sketch, "E307", {"start": v(2844.8, 762) * mm, "end": v(2743.2, 762) * mm});
            skLineSegment(sketch, "E308", {"start": v(2743.2, 762) * mm, "end": v(2641.6, 762) * mm, "construction": true});
            skLineSegment(sketch, "E309", {"start": v(2641.6, 762) * mm, "end": v(2540, 762) * mm});
            skLineSegment(sketch, "E310", {"start": v(2540, 762) * mm, "end": v(2438.4, 762) * mm, "construction": true});
            skLineSegment(sketch, "E311", {"start": v(2438.4, 762) * mm, "end": v(2336.8, 762) * mm});
            skLineSegment(sketch, "E312", {"start": v(2336.8, 762) * mm, "end": v(2235.2, 762) * mm, "construction": true});
            skLineSegment(sketch, "E313", {"start": v(2235.2, 762) * mm, "end": v(2133.6, 762) * mm});
            skLineSegment(sketch, "E314.bottom", {"start": v(2743.2, 762) * mm, "end": v(2844.8, 762) * mm});
            skLineSegment(sketch, "E314.top", {"start": v(2743.2, 254) * mm, "end": v(2844.8, 254) * mm});
            skLineSegment(sketch, "E314.left", {"start": v(2743.2, 762) * mm, "end": v(2743.2, 254) * mm});
            skLineSegment(sketch, "E314.right", {"start": v(2844.8, 762) * mm, "end": v(2844.8, 254) * mm});
            skLineSegment(sketch, "E315.top", {"start": v(2235.2, 254) * mm, "end": v(2133.6, 254) * mm});
            skLineSegment(sketch, "E315.left", {"start": v(2235.2, 762) * mm, "end": v(2235.2, 254) * mm});
            skLineSegment(sketch, "E315.right", {"start": v(2133.6, 762) * mm, "end": v(2133.6, 254) * mm});
            skLineSegment(sketch, "E316", {"start": v(2336.8, 762) * mm, "end": v(2336.8, 254) * mm});
            skLineSegment(sketch, "E317", {"start": v(2540, 762) * mm, "end": v(2540, 254) * mm});
            skLineSegment(sketch, "E318", {"start": v(2641.6, 762) * mm, "end": v(2641.6, 254) * mm});
            skLineSegment(sketch, "E319", {"start": v(2641.6, 254) * mm, "end": v(2540, 254) * mm});
            skLineSegment(sketch, "E320", {"start": v(2438.4, 762) * mm, "end": v(2438.4, 254) * mm});
            skLineSegment(sketch, "E321", {"start": v(2438.4, 254) * mm, "end": v(2336.8, 254) * mm});
            skSolve(sketch);
        }
        {
            var Q0;
            Q0 = qSketchRegion(id + "F8", true);
            extrude(context, id + "F9", {"entities" : qUnion([Q0]), "operationType" : NewBodyOperationType.REMOVE, "oppositeDirection" : true, "depth" : 101.6 * mm, "offsetDistance" : 25.4 * mm});
        }
        {
            var Q0;
            Q0=makeQuery(id+"F3.opExtrude","SWEPT_FACE",FACE,{"disambiguationData":[OSD([sQuery(id+"F2.wireOp",EDGE,"E59")])]});
            var sketch = newSketch(context, id + "F10", { "sketchPlane" : qUnion([Q0])});
            skLineSegment(sketch, "E322", {"start": v(-2540, 2082.8) * mm, "end": v(-1828.8, 2082.8) * mm});
            skLineSegment(sketch, "E323", {"start": v(-1828.8, 2082.8) * mm, "end": v(-1828.8, 863.6) * mm});
            skLineSegment(sketch, "E324", {"start": v(-1828.8, 863.6) * mm, "end": v(-2540, 863.6) * mm});
            skLineSegment(sketch, "E325", {"start": v(-2540, 863.6) * mm, "end": v(-2540, 2082.8) * mm});
            skLineSegment(sketch, "E326", {"start": v(-2540, 762) * mm, "end": v(-2438.4, 762) * mm});
            skLineSegment(sketch, "E327", {"start": v(-2438.4, 762) * mm, "end": v(-2336.8, 762) * mm, "construction": true});
            skLineSegment(sketch, "E328", {"start": v(-2336.8, 762) * mm, "end": v(-2235.2, 762) * mm});
            skLineSegment(sketch, "E329", {"start": v(-2235.2, 762) * mm, "end": v(-2133.6, 762) * mm, "construction": true});
            skLineSegment(sketch, "E330", {"start": v(-2133.6, 762) * mm, "end": v(-2032, 762) * mm});
            skLineSegment(sketch, "E331", {"start": v(-2032, 762) * mm, "end": v(-1930.4, 762) * mm, "construction": true});
            skLineSegment(sketch, "E332", {"start": v(-1930.4, 762) * mm, "end": v(-1828.8, 762) * mm});
            skLineSegment(sketch, "E333.bottom", {"start": v(-2438.4, 762) * mm, "end": v(-2540, 762) * mm});
            skLineSegment(sketch, "E333.top", {"start": v(-2438.4, 254) * mm, "end": v(-2540, 254) * mm});
            skLineSegment(sketch, "E333.left", {"start": v(-2438.4, 762) * mm, "end": v(-2438.4, 254) * mm});
            skLineSegment(sketch, "E333.right", {"start": v(-2540, 762) * mm, "end": v(-2540, 254) * mm});
            skLineSegment(sketch, "E334.top", {"start": v(-1930.4, 254) * mm, "end": v(-1828.8, 254) * mm});
            skLineSegment(sketch, "E334.left", {"start": v(-1930.4, 762) * mm, "end": v(-1930.4, 254) * mm});
            skLineSegment(sketch, "E334.right", {"start": v(-1828.8, 762) * mm, "end": v(-1828.8, 254) * mm});
            skLineSegment(sketch, "E335", {"start": v(-2032, 762) * mm, "end": v(-2032, 254) * mm});
            skLineSegment(sketch, "E336", {"start": v(-2336.8, 762) * mm, "end": v(-2336.8, 254) * mm});
            skLineSegment(sketch, "E337", {"start": v(-2235.2, 762) * mm, "end": v(-2235.2, 254) * mm});
            skLineSegment(sketch, "E338", {"start": v(-2235.2, 254) * mm, "end": v(-2336.8, 254) * mm});
            skLineSegment(sketch, "E339", {"start": v(-2133.6, 762) * mm, "end": v(-2133.6, 254) * mm});
            skLineSegment(sketch, "E340", {"start": v(-2133.6, 254) * mm, "end": v(-2032, 254) * mm});
            skSolve(sketch);
        }
        {
            var Q0;
            Q0 = qSketchRegion(id + "F10", true);
            extrude(context, id + "F11", {"entities" : qUnion([Q0]), "operationType" : NewBodyOperationType.REMOVE, "oppositeDirection" : true, "depth" : 101.6 * mm, "offsetDistance" : 25.4 * mm});
        }
        {
            var Q0;
            {var subQ39=sQuery(id+"F0.wireOp",EDGE,"E0.left");var subQ42=sQuery(id+"F0.wireOp",EDGE,"E0.bottom");var subQ49=sQuery(id+"F0.wireOp",EDGE,"E0.right");var subQ53=sQuery(id+"F0.wireOp",EDGE,"E0.top");var subQ80=makeQuery(id+"F1.opExtrude","CAP_FACE",FACE,{"disambiguationData":[OSD([subQ42,subQ53,subQ39,subQ49])],"isStart":false});var subQ82=sQuery(id+"F2.wireOp",EDGE,"E36");var subQ83=sQuery(id+"F2.wireOp",EDGE,"E38");var subQ84=sQuery(id+"F2.wireOp",EDGE,"E34");var subQ85=sQuery(id+"F2.wireOp",EDGE,"E21");var subQ86=sQuery(id+"F2.wireOp",EDGE,"E20");var subQ87=sQuery(id+"F2.wireOp",EDGE,"E22");Q0=makeQuery(id+"F5.boolean.opBoolean","MERGE",FACE,{"derivedFrom":[makeQuery(id+"F3.boolean.opBoolean","SPLIT",FACE,{"disambiguationData":[TD([makeQuery(id+"F3.opExtrude","SWEPT_FACE",FACE,{"disambiguationData":[OSD([subQ87])]})])],"derivedFrom":subQ80}),makeQuery(id+"F3.boolean.opBoolean","SPLIT",FACE,{"disambiguationData":[TD([makeQuery(id+"F3.opExtrude","SWEPT_FACE",FACE,{"disambiguationData":[OSD([subQ86])]})])],"derivedFrom":subQ80}),makeQuery(id+"F3.boolean.opBoolean","SPLIT",FACE,{"disambiguationData":[TD([makeQuery(id+"F3.opExtrude","SWEPT_FACE",FACE,{"disambiguationData":[OSD([subQ85])]})])],"derivedFrom":subQ80}),makeQuery(id+"F3.boolean.opBoolean","SPLIT",FACE,{"disambiguationData":[TD([makeQuery(id+"F3.opExtrude","SWEPT_FACE",FACE,{"disambiguationData":[OSD([subQ84])]})])],"derivedFrom":subQ80}),makeQuery(id+"F3.boolean.opBoolean","SPLIT",FACE,{"disambiguationData":[TD([makeQuery(id+"F3.opExtrude","SWEPT_FACE",FACE,{"disambiguationData":[OSD([subQ83])]})])],"derivedFrom":subQ80}),makeQuery(id+"F3.boolean.opBoolean","SPLIT",FACE,{"disambiguationData":[TD([makeQuery(id+"F3.opExtrude","SWEPT_FACE",FACE,{"disambiguationData":[OSD([subQ82])]})])],"derivedFrom":subQ80}),makeQuery(id+"F3.boolean.opBoolean","SPLIT",FACE,{"disambiguationData":[TD([makeQuery(id+"F1.opExtrude","SWEPT_FACE",FACE,{"disambiguationData":[OSD([subQ42])]})])],"derivedFrom":subQ80})],"fromTools":[makeQuery(id+"F5.opExtrude","SWEPT_FACE",FACE,{"disambiguationData":[OSD([sQuery(id+"F4.wireOp",EDGE,"E121.trimOffspring")])]}),makeQuery(id+"F5.opExtrude","SWEPT_FACE",FACE,{"disambiguationData":[OSD([sQuery(id+"F4.wireOp",EDGE,"E122.trimOffspring")])]}),makeQuery(id+"F5.opExtrude","SWEPT_FACE",FACE,{"disambiguationData":[OSD([sQuery(id+"F4.wireOp",EDGE,"E123.trimOffspring")])]}),makeQuery(id+"F5.opExtrude","SWEPT_FACE",FACE,{"disambiguationData":[OSD([sQuery(id+"F4.wireOp",EDGE,"E125")])]}),makeQuery(id+"F5.opExtrude","SWEPT_FACE",FACE,{"disambiguationData":[OSD([sQuery(id+"F4.wireOp",EDGE,"E146")])]}),makeQuery(id+"F5.opExtrude","SWEPT_FACE",FACE,{"disambiguationData":[OSD([sQuery(id+"F4.wireOp",EDGE,"E149")])]}),makeQuery(id+"F5.opExtrude","SWEPT_FACE",FACE,{"disambiguationData":[OSD([sQuery(id+"F4.wireOp",EDGE,"E152")])]}),makeQuery(id+"F5.opExtrude","SWEPT_FACE",FACE,{"disambiguationData":[OSD([sQuery(id+"F4.wireOp",EDGE,"E154")])]}),makeQuery(id+"F5.opExtrude","SWEPT_FACE",FACE,{"disambiguationData":[OSD([sQuery(id+"F4.wireOp",EDGE,"E156.top")])]}),makeQuery(id+"F5.opExtrude","SWEPT_FACE",FACE,{"disambiguationData":[OSD([sQuery(id+"F4.wireOp",EDGE,"E159")])]}),makeQuery(id+"F5.opExtrude","SWEPT_FACE",FACE,{"disambiguationData":[OSD([sQuery(id+"F4.wireOp",EDGE,"E162")])]}),makeQuery(id+"F5.opExtrude","SWEPT_FACE",FACE,{"disambiguationData":[OSD([sQuery(id+"F4.wireOp",EDGE,"E164")])]}),makeQuery(id+"F5.opExtrude","SWEPT_FACE",FACE,{"disambiguationData":[OSD([sQuery(id+"F4.wireOp",EDGE,"E168")])]}),makeQuery(id+"F5.opExtrude","SWEPT_FACE",FACE,{"disambiguationData":[OSD([sQuery(id+"F4.wireOp",EDGE,"E171")])]}),makeQuery(id+"F5.opExtrude","SWEPT_FACE",FACE,{"disambiguationData":[OSD([sQuery(id+"F4.wireOp",EDGE,"E174")])]}),makeQuery(id+"F5.opExtrude","SWEPT_FACE",FACE,{"disambiguationData":[OSD([sQuery(id+"F4.wireOp",EDGE,"E176")])]}),makeQuery(id+"F5.opExtrude","SWEPT_FACE",FACE,{"disambiguationData":[OSD([sQuery(id+"F4.wireOp",EDGE,"E178.top")])]}),makeQuery(id+"F5.opExtrude","SWEPT_FACE",FACE,{"disambiguationData":[OSD([sQuery(id+"F4.wireOp",EDGE,"E179.top")])]}),makeQuery(id+"F5.opExtrude","SWEPT_FACE",FACE,{"disambiguationData":[OSD([sQuery(id+"F4.wireOp",EDGE,"E180.top")])]}),makeQuery(id+"F5.opExtrude","SWEPT_FACE",FACE,{"disambiguationData":[OSD([sQuery(id+"F4.wireOp",EDGE,"E181.top")])]}),makeQuery(id+"F5.opExtrude","SWEPT_FACE",FACE,{"disambiguationData":[OSD([sQuery(id+"F4.wireOp",EDGE,"E186")])]}),makeQuery(id+"F5.opExtrude","SWEPT_FACE",FACE,{"disambiguationData":[OSD([sQuery(id+"F4.wireOp",EDGE,"E187")])]}),makeQuery(id+"F5.opExtrude","SWEPT_FACE",FACE,{"disambiguationData":[OSD([sQuery(id+"F4.wireOp",EDGE,"E192")])]}),makeQuery(id+"F5.opExtrude","SWEPT_FACE",FACE,{"disambiguationData":[OSD([sQuery(id+"F4.wireOp",EDGE,"E193")])]})]});}
            var sketch = newSketch(context, id + "F12", { "sketchPlane" : qUnion([Q0])});
            skLineSegment(sketch, "E341", {"start": v(-2133.6, 2743.2) * mm, "end": v(-2133.6, -1828.8) * mm});
            skLineSegment(sketch, "E342", {"start": v(3048, -1828.8) * mm, "end": v(-2133.6, -1828.8) * mm});
            skLineSegment(sketch, "E343", {"start": v(-2133.6, 2743.2) * mm, "end": v(3048, 2743.2) * mm});
            skLineSegment(sketch, "E344", {"start": v(3048, 2743.2) * mm, "end": v(3048, -1828.8) * mm});
            skSolve(sketch);
        }
        {
            var Q0;
            Q0 = qSketchRegion(id + "F12", true);
            extrude(context, id + "F13", {"entities" : qUnion([Q0]), "operationType" : NewBodyOperationType.ADD, "depth" : 4876.8 * mm, "offsetDistance" : 25.4 * mm});
        }
        {
            var Q0;
            Q0=makeQuery(id+"F13.opExtrude","SWEPT_FACE",FACE,{"disambiguationData":[OSD([sQuery(id+"F12.wireOp",EDGE,"E342")])]});
            var sketch = newSketch(context, id + "F14", { "sketchPlane" : qUnion([Q0])});
            skLineSegment(sketch, "E345", {"start": v(3048, 2082.8) * mm, "end": v(-3048, 2082.8) * mm});
            skLineSegment(sketch, "E346", {"start": v(3048, 2082.8) * mm, "end": v(3048, 2692.4) * mm});
            skLineSegment(sketch, "E347", {"start": v(3048, 2692.4) * mm, "end": v(-3048, 2692.4) * mm});
            skLineSegment(sketch, "E348", {"start": v(-3048, 2082.8) * mm, "end": v(-3048, 2692.4) * mm});
            skSolve(sketch);
        }
        {
            var Q0;
            Q0 = qSketchRegion(id + "F14", true);
            extrude(context, id + "F15", {"entities" : qUnion([Q0]), "operationType" : NewBodyOperationType.ADD, "depth" : 914.4 * mm, "offsetDistance" : 25.4 * mm});
        }
        {
            var Q0;
            Q0=makeQuery(id+"F13.opExtrude","SWEPT_FACE",FACE,{"disambiguationData":[OSD([sQuery(id+"F12.wireOp",EDGE,"E341")])]});
            var sketch = newSketch(context, id + "F16", { "sketchPlane" : qUnion([Q0])});
            skLineSegment(sketch, "E349", {"start": v(1828.8, 2082.8) * mm, "end": v(-2743.2, 2082.8) * mm});
            skLineSegment(sketch, "E350", {"start": v(1828.8, 2692.4) * mm, "end": v(-2743.2, 2692.4) * mm});
            skLineSegment(sketch, "E351", {"start": v(-2743.2, 2692.4) * mm, "end": v(-2743.2, 2082.8) * mm});
            skLineSegment(sketch, "E352", {"start": v(1828.8, 2082.8) * mm, "end": v(1828.8, 2692.4) * mm});
            skSolve(sketch);
        }
        {
            var Q0;
            Q0 = qSketchRegion(id + "F16", true);
            extrude(context, id + "F17", {"entities" : qUnion([Q0]), "operationType" : NewBodyOperationType.ADD, "depth" : 914.4 * mm, "offsetDistance" : 25.4 * mm});
        }
        {
            var Q0;
            Q0=makeQuery(id+"F17.boolean.opBoolean","MERGE",FACE,{"derivedFrom":[makeQuery(id+"F13.boolean.opBoolean","MERGE",FACE,{"derivedFrom":[makeQuery(id+"F3.boolean.opBoolean","MERGE",FACE,{"derivedFrom":[makeQuery(id+"F1.opExtrude","SWEPT_FACE",FACE,{"disambiguationData":[OSD([sQuery(id+"F0.wireOp",EDGE,"E0.bottom")])]}),makeQuery(id+"F3.opExtrude","SWEPT_FACE",FACE,{"disambiguationData":[OSD([sQuery(id+"F2.wireOp",EDGE,"E55.bottom")])]})]}),makeQuery(id+"F13.opExtrude","SWEPT_FACE",FACE,{"disambiguationData":[OSD([sQuery(id+"F12.wireOp",EDGE,"E343")])]})]}),makeQuery(id+"F17.opExtrude","SWEPT_FACE",FACE,{"disambiguationData":[OSD([sQuery(id+"F16.wireOp",EDGE,"E351")])]})]});
            var sketch = newSketch(context, id + "F18", { "sketchPlane" : qUnion([Q0])});
            skLineSegment(sketch, "E353", {"start": v(2133.6, 2692.4) * mm, "end": v(3048, 2184.4) * mm});
            skLineSegment(sketch, "E354", {"start": v(3048, 2184.4) * mm, "end": v(3048, 2692.4) * mm});
            skLineSegment(sketch, "E355", {"start": v(3048, 2692.4) * mm, "end": v(2133.6, 2692.4) * mm});
            skSolve(sketch);
        }
        {
            var Q0;
            Q0 = qSketchRegion(id + "F18", true);
            extrude(context, id + "F19", {"entities" : qUnion([Q0]), "operationType" : NewBodyOperationType.REMOVE, "endBound" : BoundingType.THROUGH_ALL, "oppositeDirection" : true, "depth" : 25.4 * mm, "offsetDistance" : 25.4 * mm});
        }
        {
            var Q0;
            Q0=makeQuery(id+"F15.boolean.opBoolean","MERGE",FACE,{"derivedFrom":[makeQuery(id+"F13.boolean.opBoolean","MERGE",FACE,{"derivedFrom":[makeQuery(id+"F3.boolean.opBoolean","MERGE",FACE,{"derivedFrom":[makeQuery(id+"F1.opExtrude","SWEPT_FACE",FACE,{"disambiguationData":[OSD([sQuery(id+"F0.wireOp",EDGE,"E0.right")])]}),makeQuery(id+"F3.opExtrude","SWEPT_FACE",FACE,{"disambiguationData":[OSD([sQuery(id+"F2.wireOp",EDGE,"E7")])]})]}),makeQuery(id+"F13.opExtrude","SWEPT_FACE",FACE,{"disambiguationData":[OSD([sQuery(id+"F12.wireOp",EDGE,"E344")])]})]}),makeQuery(id+"F15.opExtrude","SWEPT_FACE",FACE,{"disambiguationData":[OSD([sQuery(id+"F14.wireOp",EDGE,"E346")])]})]});
            var sketch = newSketch(context, id + "F20", { "sketchPlane" : qUnion([Q0])});
            skLineSegment(sketch, "E356", {"start": v(-1828.8, 2692.4) * mm, "end": v(-2743.2, 2184.4) * mm});
            skLineSegment(sketch, "E357", {"start": v(-2743.2, 2184.4) * mm, "end": v(-2743.2, 2692.4) * mm});
            skLineSegment(sketch, "E358", {"start": v(-2743.2, 2692.4) * mm, "end": v(-1828.8, 2692.4) * mm});
            skSolve(sketch);
        }
        {
            var Q0;
            Q0 = qSketchRegion(id + "F20", true);
            extrude(context, id + "F21", {"entities" : qUnion([Q0]), "operationType" : NewBodyOperationType.REMOVE, "endBound" : BoundingType.THROUGH_ALL, "oppositeDirection" : true, "depth" : 25.4 * mm, "offsetDistance" : 25.4 * mm});
        }
        {
            var Q0;
            Q0=makeQuery(id+"F17.boolean.opBoolean","MERGE",FACE,{"derivedFrom":[makeQuery(id+"F13.boolean.opBoolean","MERGE",FACE,{"derivedFrom":[makeQuery(id+"F3.boolean.opBoolean","MERGE",FACE,{"derivedFrom":[makeQuery(id+"F1.opExtrude","SWEPT_FACE",FACE,{"disambiguationData":[OSD([sQuery(id+"F0.wireOp",EDGE,"E0.bottom")])]}),makeQuery(id+"F3.opExtrude","SWEPT_FACE",FACE,{"disambiguationData":[OSD([sQuery(id+"F2.wireOp",EDGE,"E55.bottom")])]})]}),makeQuery(id+"F13.opExtrude","SWEPT_FACE",FACE,{"disambiguationData":[OSD([sQuery(id+"F12.wireOp",EDGE,"E343")])]})]}),makeQuery(id+"F17.opExtrude","SWEPT_FACE",FACE,{"disambiguationData":[OSD([sQuery(id+"F16.wireOp",EDGE,"E351")])]})]});
            var sketch = newSketch(context, id + "F22", { "sketchPlane" : qUnion([Q0])});
            skLineSegment(sketch, "E359", {"start": v(3048, 2184.4) * mm, "end": v(-3048, 2184.4) * mm, "construction": true});
            skLineSegment(sketch, "E360", {"start": v(2133.6, 2692.4) * mm, "end": v(-3048, 2692.4) * mm, "construction": true});
            skLineSegment(sketch, "E361", {"start": v(-3048, 2184.4) * mm, "end": v(-2133.6, 2692.4) * mm});
            skLineSegment(sketch, "E362", {"start": v(-2133.6, 2692.4) * mm, "end": v(-2133.6, 5130.8) * mm});
            skLineSegment(sketch, "E363", {"start": v(-2133.6, 5130.8) * mm, "end": v(-3048, 5130.8) * mm});
            skLineSegment(sketch, "E364", {"start": v(-3048, 5130.8) * mm, "end": v(-3048, 2184.4) * mm});
            skSolve(sketch);
        }
        {
            var Q0;
            Q0=makeQuery(id+"F15.boolean.opBoolean","MERGE",FACE,{"derivedFrom":[makeQuery(id+"F13.boolean.opBoolean","MERGE",FACE,{"derivedFrom":[makeQuery(id+"F3.boolean.opBoolean","MERGE",FACE,{"derivedFrom":[makeQuery(id+"F1.opExtrude","SWEPT_FACE",FACE,{"disambiguationData":[OSD([sQuery(id+"F0.wireOp",EDGE,"E0.right")])]}),makeQuery(id+"F3.opExtrude","SWEPT_FACE",FACE,{"disambiguationData":[OSD([sQuery(id+"F2.wireOp",EDGE,"E7")])]})]}),makeQuery(id+"F13.opExtrude","SWEPT_FACE",FACE,{"disambiguationData":[OSD([sQuery(id+"F12.wireOp",EDGE,"E344")])]})]}),makeQuery(id+"F15.opExtrude","SWEPT_FACE",FACE,{"disambiguationData":[OSD([sQuery(id+"F14.wireOp",EDGE,"E346")])]})]});
            var sketch = newSketch(context, id + "F23", { "sketchPlane" : qUnion([Q0])});
            skLineSegment(sketch, "E365", {"start": v(-2743.2, 2184.4) * mm, "end": v(2743.2, 2184.4) * mm, "construction": true});
            skLineSegment(sketch, "E366", {"start": v(-1828.8, 2692.4) * mm, "end": v(2743.2, 2692.4) * mm, "construction": true});
            skLineSegment(sketch, "E367", {"start": v(2743.2, 2184.4) * mm, "end": v(1828.8, 2692.4) * mm});
            skLineSegment(sketch, "E368", {"start": v(1828.8, 2692.4) * mm, "end": v(1828.8, 5130.8) * mm});
            skLineSegment(sketch, "E369", {"start": v(1828.8, 5130.8) * mm, "end": v(2743.2, 5130.8) * mm});
            skLineSegment(sketch, "E370", {"start": v(2743.2, 5130.8) * mm, "end": v(2743.2, 2184.4) * mm});
            skSolve(sketch);
        }
        {
            var Q0;
            Q0 = qSketchRegion(id + "F22", true);
            extrude(context, id + "F24", {"entities" : qUnion([Q0]), "operationType" : NewBodyOperationType.REMOVE, "endBound" : BoundingType.THROUGH_ALL, "oppositeDirection" : true, "depth" : 25.4 * mm, "offsetDistance" : 25.4 * mm});
        }
        {
            var Q0;
            Q0 = qSketchRegion(id + "F23", true);
            extrude(context, id + "F25", {"entities" : qUnion([Q0]), "operationType" : NewBodyOperationType.REMOVE, "endBound" : BoundingType.THROUGH_ALL, "oppositeDirection" : true, "depth" : 25.4 * mm, "offsetDistance" : 25.4 * mm});
        }
        {
            var Q0;
            {var subQ3=sQuery(id+"F12.wireOp",EDGE,"E342");var subQ4=sQuery(id+"F14.wireOp",EDGE,"E347");Q0=makeQuery(id+"F15.boolean.opBoolean","SPLIT",FACE,{"disambiguationData":[TD([makeQuery(id+"F15.opExtrude","SWEPT_FACE",FACE,{"disambiguationData":[OSD([subQ4])]})])],"derivedFrom":makeQuery(id+"F13.opExtrude","SWEPT_FACE",FACE,{"disambiguationData":[OSD([subQ3])]})});}
            var sketch = newSketch(context, id + "F26", { "sketchPlane" : qUnion([Q0])});
            skLineSegment(sketch, "E371", {"start": v(-2133.6, 2692.4) * mm, "end": v(0, 5130.8) * mm});
            skLineSegment(sketch, "E372", {"start": v(0, 5130.8) * mm, "end": v(2133.6, 2692.4) * mm});
            skLineSegment(sketch, "E373", {"start": v(-2133.6, 2692.4) * mm, "end": v(2133.6, 2692.4) * mm});
            skSolve(sketch);
        }
        {
            var Q0;
            {var subQ2=sQuery(id+"F12.wireOp",EDGE,"E341");Q0=makeQuery(id+"F17.boolean.opBoolean","SPLIT",FACE,{"disambiguationData":[TD([makeQuery(id+"F15.opExtrude","SWEPT_FACE",FACE,{"disambiguationData":[OSD([sQuery(id+"F14.wireOp",EDGE,"E347")])]})])],"derivedFrom":makeQuery(id+"F13.opExtrude","SWEPT_FACE",FACE,{"disambiguationData":[OSD([subQ2])]})});}
            var sketch = newSketch(context, id + "F27", { "sketchPlane" : qUnion([Q0])});
            skLineSegment(sketch, "E374", {"start": v(1828.8, 2692.4) * mm, "end": v(0, 5130.8) * mm});
            skLineSegment(sketch, "E375", {"start": v(0, 5130.8) * mm, "end": v(1828.8, 5130.8) * mm});
            skLineSegment(sketch, "E376", {"start": v(1828.8, 5130.8) * mm, "end": v(1828.8, 2692.4) * mm});
            skLineSegment(sketch, "E377", {"start": v(0, 5130.8) * mm, "end": v(-1828.8, 2692.4) * mm});
            skLineSegment(sketch, "E378", {"start": v(-1828.8, 2692.4) * mm, "end": v(-1828.8, 5130.8) * mm});
            skLineSegment(sketch, "E379", {"start": v(-1828.8, 5130.8) * mm, "end": v(0, 5130.8) * mm});
            skSolve(sketch);
        }
        {
            var Q0;
            Q0 = qSketchRegion(id + "F27", true);
            extrude(context, id + "F28", {"entities" : qUnion([Q0]), "operationType" : NewBodyOperationType.REMOVE, "endBound" : BoundingType.THROUGH_ALL, "oppositeDirection" : true, "depth" : 2133.6 * mm, "offsetDistance" : 25.4 * mm});
        }
        {
            var Q0;
            Q0 = qSketchRegion(id + "F26", true);
            extrude(context, id + "F29", {"entities" : qUnion([Q0]), "operationType" : NewBodyOperationType.ADD, "oppositeDirection" : true, "depth" : 1828.8 * mm, "offsetDistance" : 25.4 * mm});
        }
        {
            var Q0;
            {var subQ2=sQuery(id+"F12.wireOp",EDGE,"E341");Q0=makeQuery(id+"F17.boolean.opBoolean","SPLIT",FACE,{"disambiguationData":[TD([makeQuery(id+"F15.opExtrude","SWEPT_FACE",FACE,{"disambiguationData":[OSD([sQuery(id+"F14.wireOp",EDGE,"E347")])]})])],"derivedFrom":makeQuery(id+"F13.opExtrude","SWEPT_FACE",FACE,{"disambiguationData":[OSD([subQ2])]})});}
            var sketch = newSketch(context, id + "F30", { "sketchPlane" : qUnion([Q0])});
            skLineSegment(sketch, "E380.bottom", {"start": v(-152.4, 2235.2) * mm, "end": v(152.4, 2235.2) * mm});
            skLineSegment(sketch, "E380.top", {"start": v(-152.4, 5706.01) * mm, "end": v(152.4, 5706.01) * mm});
            skLineSegment(sketch, "E380.left", {"start": v(-152.4, 2235.2) * mm, "end": v(-152.4, 5706.01) * mm});
            skLineSegment(sketch, "E380.right", {"start": v(152.4, 2235.2) * mm, "end": v(152.4, 5706.01) * mm});
            skLineSegment(sketch, "E381", {"start": v(0, 2692.4) * mm, "end": v(0, 3238.94) * mm, "construction": true});
            skSolve(sketch);
        }
        {
            var Q0;
            Q0 = qSketchRegion(id + "F30", true);
            extrude(context, id + "F31", {"entities" : qUnion([Q0]), "operationType" : NewBodyOperationType.ADD, "depth" : 304.8 * mm, "offsetDistance" : 25.4 * mm});
        }
        {
            var Q0;
            Q0=makeQuery(id+"F15.boolean.opBoolean","SPLIT",FACE,{"disambiguationData":[TD([makeQuery(id+"F3.opExtrude","SWEPT_FACE",FACE,{"disambiguationData":[OSD([sQuery(id+"F2.wireOp",EDGE,"E59")])]})])],"derivedFrom":makeQuery(id+"F13.opExtrude","SWEPT_FACE",FACE,{"disambiguationData":[OSD([sQuery(id+"F12.wireOp",EDGE,"E342")])]})});
            var sketch = newSketch(context, id + "F32", { "sketchPlane" : qUnion([Q0])});
            skLineSegment(sketch, "E382.0", {"start": v(-457.2, 1778) * mm, "end": v(-457.2, 254) * mm});
            skLineSegment(sketch, "E382.1", {"start": v(-457.2, 254) * mm, "end": v(457.2, 254) * mm});
            skLineSegment(sketch, "E382.2", {"start": v(457.2, 1778) * mm, "end": v(457.2, 254) * mm});
            skLineSegment(sketch, "E383", {"start": v(0, 254) * mm, "end": v(0, 2082.8) * mm, "construction": true});
            skLineSegment(sketch, "E384.bottom", {"start": v(-374.85, 254) * mm, "end": v(288.38, 254) * mm});
            skLineSegment(sketch, "E385", {"start": v(-457.2, 1778) * mm, "end": v(457.2, 1778) * mm});
            skSolve(sketch);
        }
        {
            var Q0;
            Q0 = qSketchRegion(id + "F32", true);
            extrude(context, id + "F33", {"entities" : qUnion([Q0]), "depth" : 50.8 * mm, "offsetDistance" : 25.4 * mm});
        }
        {
            var Q0;
            Q0=makeQuery(id+"F17.boolean.opBoolean","SPLIT",FACE,{"disambiguationData":[TD([makeQuery(id+"F3.opExtrude","SWEPT_FACE",FACE,{"disambiguationData":[OSD([sQuery(id+"F2.wireOp",EDGE,"E62")])]})])],"derivedFrom":makeQuery(id+"F13.opExtrude","SWEPT_FACE",FACE,{"disambiguationData":[OSD([sQuery(id+"F12.wireOp",EDGE,"E341")])]})});
            var sketch = newSketch(context, id + "F34", { "sketchPlane" : qUnion([Q0])});
            skLineSegment(sketch, "E386.0", {"start": v(457.2, 1778) * mm, "end": v(457.2, 254) * mm});
            skLineSegment(sketch, "E386.1", {"start": v(-457.2, 254) * mm, "end": v(457.2, 254) * mm});
            skLineSegment(sketch, "E386.2", {"start": v(-457.2, 1778) * mm, "end": v(-457.2, 254) * mm});
            skLineSegment(sketch, "E387", {"start": v(-457.2, 1778) * mm, "end": v(457.2, 1778) * mm});
            skSolve(sketch);
        }
        {
            var Q0;
            Q0 = qSketchRegion(id + "F34", true);
            extrude(context, id + "F35", {"entities" : qUnion([Q0]), "depth" : 50.8 * mm, "offsetDistance" : 25.4 * mm});
        }
        {
            var Q0;
            Q0=makeQuery(id+"F29.opExtrude","CAP_FACE",FACE,{"disambiguationData":[OSD([sQuery(id+"F26.wireOp",EDGE,"E371"),sQuery(id+"F26.wireOp",EDGE,"E372"),sQuery(id+"F26.wireOp",EDGE,"E373")])],"isStart":true});
            var sketch = newSketch(context, id + "F36", { "sketchPlane" : qUnion([Q0])});
            skLineSegment(sketch, "E388", {"start": v(0, 2692.4) * mm, "end": v(0, 5130.8) * mm, "construction": true});
            skLineSegment(sketch, "E389.bottom", {"start": v(-457.2, 2844.8) * mm, "end": v(-50.8, 2844.8) * mm});
            skLineSegment(sketch, "E389.top", {"start": v(-457.2, 4064) * mm, "end": v(-50.8, 4064) * mm});
            skLineSegment(sketch, "E389.left", {"start": v(-457.2, 2844.8) * mm, "end": v(-457.2, 3403.6) * mm});
            skLineSegment(sketch, "E389.right", {"start": v(457.2, 2844.8) * mm, "end": v(457.2, 3403.6) * mm});
            skLineSegment(sketch, "E390", {"start": v(-50.8, 4064) * mm, "end": v(-50.8, 3505.2) * mm});
            skLineSegment(sketch, "E391", {"start": v(50.8, 4064) * mm, "end": v(50.8, 3505.2) * mm});
            skLineSegment(sketch, "E392.trimOffspring", {"start": v(50.8, 4064) * mm, "end": v(457.2, 4064) * mm});
            skLineSegment(sketch, "E393.trimOffspring", {"start": v(50.8, 2844.8) * mm, "end": v(457.2, 2844.8) * mm});
            skLineSegment(sketch, "E394", {"start": v(457.2, 3454.4) * mm, "end": v(-457.2, 3454.4) * mm, "construction": true});
            skLineSegment(sketch, "E395", {"start": v(-457.2, 3505.2) * mm, "end": v(-50.8, 3505.2) * mm});
            skLineSegment(sketch, "E396", {"start": v(457.2, 3403.6) * mm, "end": v(50.8, 3403.6) * mm});
            skLineSegment(sketch, "E397.trimOffspring", {"start": v(-457.2, 3505.2) * mm, "end": v(-457.2, 4064) * mm});
            skLineSegment(sketch, "E398.trimOffspring", {"start": v(-50.8, 3403.6) * mm, "end": v(-457.2, 3403.6) * mm});
            skLineSegment(sketch, "E399.trimOffspring", {"start": v(457.2, 3505.2) * mm, "end": v(457.2, 4064) * mm});
            skLineSegment(sketch, "E400.trimOffspring", {"start": v(50.8, 3505.2) * mm, "end": v(457.2, 3505.2) * mm});
            skLineSegment(sketch, "E401.trimOffspring", {"start": v(-50.8, 3403.6) * mm, "end": v(-50.8, 2844.8) * mm});
            skLineSegment(sketch, "E402.trimOffspring", {"start": v(50.8, 3403.6) * mm, "end": v(50.8, 2844.8) * mm});
            skLineSegment(sketch, "E403", {"start": v(-457.2, 4064) * mm, "end": v(-457.2, 4165.6) * mm, "construction": true});
            skLineSegment(sketch, "E404", {"start": v(-457.2, 4165.6) * mm, "end": v(457.2, 4165.6) * mm});
            skLineSegment(sketch, "E405", {"start": v(457.2, 4064) * mm, "end": v(457.2, 4165.6) * mm, "construction": true});
            skArc(sketch, "E406", {"start": v(457.2, 4165.6) * mm, "mid": v(0, 4419.6) * mm, "end": v(-457.2, 4165.6) * mm});
            skSolve(sketch);
        }
        {
            var Q0;
            Q0 = qSketchRegion(id + "F36", true);
            extrude(context, id + "F37", {"entities" : qUnion([Q0]), "operationType" : NewBodyOperationType.REMOVE, "oppositeDirection" : true, "depth" : 50.8 * mm, "offsetDistance" : 25.4 * mm});
        }
        {
            var Q0;
            Q0=makeQuery(id+"F15.boolean.opBoolean","SPLIT",FACE,{"disambiguationData":[TD([makeQuery(id+"F3.opExtrude","SWEPT_FACE",FACE,{"disambiguationData":[OSD([sQuery(id+"F2.wireOp",EDGE,"E59")])]})])],"derivedFrom":makeQuery(id+"F13.opExtrude","SWEPT_FACE",FACE,{"disambiguationData":[OSD([sQuery(id+"F12.wireOp",EDGE,"E342")])]})});
            var sketch = newSketch(context, id + "F38", { "sketchPlane" : qUnion([Q0])});
            skLineSegment(sketch, "E407", {"start": v(2743.2, 1778) * mm, "end": v(1803.4, 1778) * mm});
            skLineSegment(sketch, "E408", {"start": v(2743.2, 1778) * mm, "end": v(2743.2, 863.6) * mm});
            skLineSegment(sketch, "E409", {"start": v(2743.2, 863.6) * mm, "end": v(1803.4, 863.6) * mm});
            skLineSegment(sketch, "E410", {"start": v(762, 1778) * mm, "end": v(762, 863.6) * mm});
            skLineSegment(sketch, "E411", {"start": v(1752.6, 1778) * mm, "end": v(1752.6, 863.6) * mm, "construction": true});
            skLineSegment(sketch, "E412", {"start": v(1701.8, 1778) * mm, "end": v(1701.8, 863.6) * mm});
            skLineSegment(sketch, "E413", {"start": v(1803.4, 863.6) * mm, "end": v(1803.4, 1778) * mm});
            skLineSegment(sketch, "E414.trimOffspring", {"start": v(1701.8, 1778) * mm, "end": v(762, 1778) * mm});
            skLineSegment(sketch, "E415.trimOffspring", {"start": v(1701.8, 863.6) * mm, "end": v(762, 863.6) * mm});
            skLineSegment(sketch, "E416", {"start": v(762, 1778) * mm, "end": v(-762, 1778) * mm, "construction": true});
            skLineSegment(sketch, "E417", {"start": v(-762, 1778) * mm, "end": v(-1913.47, 1778) * mm});
            skLineSegment(sketch, "E418", {"start": v(762, 863.6) * mm, "end": v(-762, 863.6) * mm, "construction": true});
            skLineSegment(sketch, "E419", {"start": v(-762, 863.6) * mm, "end": v(-762, 1778) * mm});
            skLineSegment(sketch, "E420", {"start": v(-762, 863.6) * mm, "end": v(-1913.47, 863.6) * mm});
            skLineSegment(sketch, "E421", {"start": v(-1913.47, 1778) * mm, "end": v(-1913.47, 863.6) * mm});
            skPoint(sketch, "E422.orphan", {"position": v(-1919.36, 863.6) * mm});
            skSolve(sketch);
        }
        {
            var Q0;
            Q0 = qSketchRegion(id + "F38", true);
            extrude(context, id + "F39", {"entities" : qUnion([Q0]), "operationType" : NewBodyOperationType.REMOVE, "oppositeDirection" : true, "depth" : 50.8 * mm, "offsetDistance" : 25.4 * mm});
        }
        {
            var Q0;
            Q0=makeQuery(id+"F17.boolean.opBoolean","SPLIT",FACE,{"disambiguationData":[TD([makeQuery(id+"F3.opExtrude","SWEPT_FACE",FACE,{"disambiguationData":[OSD([sQuery(id+"F2.wireOp",EDGE,"E62")])]})])],"derivedFrom":makeQuery(id+"F13.opExtrude","SWEPT_FACE",FACE,{"disambiguationData":[OSD([sQuery(id+"F12.wireOp",EDGE,"E341")])]})});
            var sketch = newSketch(context, id + "F40", { "sketchPlane" : qUnion([Q0])});
            skLineSegment(sketch, "E423.bottom", {"start": v(-2438.4, 1778) * mm, "end": v(-1603.62, 1778) * mm});
            skLineSegment(sketch, "E423.top", {"start": v(-2438.4, 863.6) * mm, "end": v(-1603.62, 863.6) * mm});
            skLineSegment(sketch, "E423.left", {"start": v(-2438.4, 1778) * mm, "end": v(-2438.4, 863.6) * mm});
            skLineSegment(sketch, "E423.right", {"start": v(-1603.62, 1778) * mm, "end": v(-1603.62, 863.6) * mm});
            skLineSegment(sketch, "E424.bottom", {"start": v(-762, 1778) * mm, "end": v(-1502.02, 1778) * mm});
            skLineSegment(sketch, "E424.top", {"start": v(-762, 863.6) * mm, "end": v(-1502.02, 863.6) * mm});
            skLineSegment(sketch, "E424.left", {"start": v(-762, 1778) * mm, "end": v(-762, 863.6) * mm});
            skLineSegment(sketch, "E424.right", {"start": v(-1502.02, 1778) * mm, "end": v(-1502.02, 863.6) * mm});
            skLineSegment(sketch, "E425.bottom", {"start": v(762, 1778) * mm, "end": v(1710.27, 1778) * mm});
            skLineSegment(sketch, "E425.top", {"start": v(762, 863.6) * mm, "end": v(1710.27, 863.6) * mm});
            skLineSegment(sketch, "E425.left", {"start": v(762, 1778) * mm, "end": v(762, 863.6) * mm});
            skLineSegment(sketch, "E425.right", {"start": v(1710.27, 1778) * mm, "end": v(1710.27, 863.6) * mm});
            skSolve(sketch);
        }
        {
            var Q0;
            Q0 = qSketchRegion(id + "F40", true);
            extrude(context, id + "F41", {"entities" : qUnion([Q0]), "operationType" : NewBodyOperationType.REMOVE, "oppositeDirection" : true, "depth" : 50.8 * mm, "offsetDistance" : 25.4 * mm});
        }
        {
            var Q0;
            {var subQ5=sQuery(id+"F0.wireOp",EDGE,"E0.left");var subQ17=sQuery(id+"F0.wireOp",EDGE,"E0.bottom");var subQ63=sQuery(id+"F2.wireOp",EDGE,"E38");var subQ64=makeQuery(id+"F3.opExtrude","SWEPT_FACE",FACE,{"disambiguationData":[OSD([subQ63])]});var subQ65=sQuery(id+"F2.wireOp",EDGE,"E36");var subQ66=makeQuery(id+"F3.opExtrude","SWEPT_FACE",FACE,{"disambiguationData":[OSD([subQ65])]});var subQ67=sQuery(id+"F2.wireOp",EDGE,"E34");var subQ68=makeQuery(id+"F3.opExtrude","SWEPT_FACE",FACE,{"disambiguationData":[OSD([subQ67])]});var subQ73=sQuery(id+"F0.wireOp",EDGE,"E0.top");var subQ86=sQuery(id+"F2.wireOp",EDGE,"E21");var subQ100=sQuery(id+"F2.wireOp",EDGE,"E20");var subQ116=sQuery(id+"F0.wireOp",EDGE,"E0.right");var subQ124=sQuery(id+"F2.wireOp",EDGE,"E22");var subQ128=makeQuery(id+"F1.opExtrude","SWEPT_FACE",FACE,{"disambiguationData":[OSD([subQ73])]});var subQ146=makeQuery(id+"F3.opExtrude","SWEPT_FACE",FACE,{"disambiguationData":[OSD([subQ100])]});var subQ147=makeQuery(id+"F3.opExtrude","SWEPT_FACE",FACE,{"disambiguationData":[OSD([subQ86])]});var subQ148=makeQuery(id+"F3.opExtrude","SWEPT_FACE",FACE,{"disambiguationData":[OSD([subQ124])]});var subQ187=makeQuery(id+"F1.opExtrude","CAP_FACE",FACE,{"disambiguationData":[OSD([subQ17,subQ73,subQ5,subQ116])],"isStart":false});Q0=makeQuery(id+"F13.boolean.opBoolean","SPLIT",FACE,{"disambiguationData":[TD([subQ128])],"derivedFrom":makeQuery(id+"F5.boolean.opBoolean","MERGE",FACE,{"derivedFrom":[makeQuery(id+"F3.boolean.opBoolean","SPLIT",FACE,{"disambiguationData":[TD([subQ148])],"derivedFrom":subQ187}),makeQuery(id+"F3.boolean.opBoolean","SPLIT",FACE,{"disambiguationData":[TD([subQ146])],"derivedFrom":subQ187}),makeQuery(id+"F3.boolean.opBoolean","SPLIT",FACE,{"disambiguationData":[TD([subQ147])],"derivedFrom":subQ187}),makeQuery(id+"F3.boolean.opBoolean","SPLIT",FACE,{"disambiguationData":[TD([subQ68])],"derivedFrom":subQ187}),makeQuery(id+"F3.boolean.opBoolean","SPLIT",FACE,{"disambiguationData":[TD([subQ64])],"derivedFrom":subQ187}),makeQuery(id+"F3.boolean.opBoolean","SPLIT",FACE,{"disambiguationData":[TD([subQ66])],"derivedFrom":subQ187}),makeQuery(id+"F3.boolean.opBoolean","SPLIT",FACE,{"disambiguationData":[TD([makeQuery(id+"F1.opExtrude","SWEPT_FACE",FACE,{"disambiguationData":[OSD([subQ17])]})])],"derivedFrom":subQ187})],"fromTools":[makeQuery(id+"F5.opExtrude","SWEPT_FACE",FACE,{"disambiguationData":[OSD([sQuery(id+"F4.wireOp",EDGE,"E121.trimOffspring")])]}),makeQuery(id+"F5.opExtrude","SWEPT_FACE",FACE,{"disambiguationData":[OSD([sQuery(id+"F4.wireOp",EDGE,"E122.trimOffspring")])]}),makeQuery(id+"F5.opExtrude","SWEPT_FACE",FACE,{"disambiguationData":[OSD([sQuery(id+"F4.wireOp",EDGE,"E123.trimOffspring")])]}),makeQuery(id+"F5.opExtrude","SWEPT_FACE",FACE,{"disambiguationData":[OSD([sQuery(id+"F4.wireOp",EDGE,"E125")])]}),makeQuery(id+"F5.opExtrude","SWEPT_FACE",FACE,{"disambiguationData":[OSD([sQuery(id+"F4.wireOp",EDGE,"E146")])]}),makeQuery(id+"F5.opExtrude","SWEPT_FACE",FACE,{"disambiguationData":[OSD([sQuery(id+"F4.wireOp",EDGE,"E149")])]}),makeQuery(id+"F5.opExtrude","SWEPT_FACE",FACE,{"disambiguationData":[OSD([sQuery(id+"F4.wireOp",EDGE,"E152")])]}),makeQuery(id+"F5.opExtrude","SWEPT_FACE",FACE,{"disambiguationData":[OSD([sQuery(id+"F4.wireOp",EDGE,"E154")])]}),makeQuery(id+"F5.opExtrude","SWEPT_FACE",FACE,{"disambiguationData":[OSD([sQuery(id+"F4.wireOp",EDGE,"E156.top")])]}),makeQuery(id+"F5.opExtrude","SWEPT_FACE",FACE,{"disambiguationData":[OSD([sQuery(id+"F4.wireOp",EDGE,"E159")])]}),makeQuery(id+"F5.opExtrude","SWEPT_FACE",FACE,{"disambiguationData":[OSD([sQuery(id+"F4.wireOp",EDGE,"E162")])]}),makeQuery(id+"F5.opExtrude","SWEPT_FACE",FACE,{"disambiguationData":[OSD([sQuery(id+"F4.wireOp",EDGE,"E164")])]}),makeQuery(id+"F5.opExtrude","SWEPT_FACE",FACE,{"disambiguationData":[OSD([sQuery(id+"F4.wireOp",EDGE,"E168")])]}),makeQuery(id+"F5.opExtrude","SWEPT_FACE",FACE,{"disambiguationData":[OSD([sQuery(id+"F4.wireOp",EDGE,"E171")])]}),makeQuery(id+"F5.opExtrude","SWEPT_FACE",FACE,{"disambiguationData":[OSD([sQuery(id+"F4.wireOp",EDGE,"E174")])]}),makeQuery(id+"F5.opExtrude","SWEPT_FACE",FACE,{"disambiguationData":[OSD([sQuery(id+"F4.wireOp",EDGE,"E176")])]}),makeQuery(id+"F5.opExtrude","SWEPT_FACE",FACE,{"disambiguationData":[OSD([sQuery(id+"F4.wireOp",EDGE,"E178.top")])]}),makeQuery(id+"F5.opExtrude","SWEPT_FACE",FACE,{"disambiguationData":[OSD([sQuery(id+"F4.wireOp",EDGE,"E179.top")])]}),makeQuery(id+"F5.opExtrude","SWEPT_FACE",FACE,{"disambiguationData":[OSD([sQuery(id+"F4.wireOp",EDGE,"E180.top")])]}),makeQuery(id+"F5.opExtrude","SWEPT_FACE",FACE,{"disambiguationData":[OSD([sQuery(id+"F4.wireOp",EDGE,"E181.top")])]}),makeQuery(id+"F5.opExtrude","SWEPT_FACE",FACE,{"disambiguationData":[OSD([sQuery(id+"F4.wireOp",EDGE,"E186")])]}),makeQuery(id+"F5.opExtrude","SWEPT_FACE",FACE,{"disambiguationData":[OSD([sQuery(id+"F4.wireOp",EDGE,"E187")])]}),makeQuery(id+"F5.opExtrude","SWEPT_FACE",FACE,{"disambiguationData":[OSD([sQuery(id+"F4.wireOp",EDGE,"E192")])]}),makeQuery(id+"F5.opExtrude","SWEPT_FACE",FACE,{"disambiguationData":[OSD([sQuery(id+"F4.wireOp",EDGE,"E193")])]})]})});}
            var sketch = newSketch(context, id + "F42", { "sketchPlane" : qUnion([Q0])});
            skLineSegment(sketch, "E426.bottom", {"start": v(-3048, 457.2) * mm, "end": v(-2844.8, 457.2) * mm});
            skLineSegment(sketch, "E426.top", {"start": v(-3048, -457.2) * mm, "end": v(-2844.8, -457.2) * mm});
            skLineSegment(sketch, "E426.left", {"start": v(-3048, 457.2) * mm, "end": v(-3048, -457.2) * mm});
            skLineSegment(sketch, "E426.right", {"start": v(-2844.8, 457.2) * mm, "end": v(-2844.8, -457.2) * mm});
            skLineSegment(sketch, "E427.bottom", {"start": v(-457.2, -2540) * mm, "end": v(457.2, -2540) * mm});
            skLineSegment(sketch, "E427.top", {"start": v(-457.2, -2743.2) * mm, "end": v(457.2, -2743.2) * mm});
            skLineSegment(sketch, "E427.left", {"start": v(-457.2, -2540) * mm, "end": v(-457.2, -2743.2) * mm});
            skLineSegment(sketch, "E427.right", {"start": v(457.2, -2540) * mm, "end": v(457.2, -2743.2) * mm});
            skSolve(sketch);
        }
        {
            var Q0;
            Q0 = qSketchRegion(id + "F42", true);
            extrude(context, id + "F43", {"entities" : qUnion([Q0]), "operationType" : NewBodyOperationType.REMOVE, "oppositeDirection" : true, "depth" : 152.4 * mm, "offsetDistance" : 25.4 * mm});
        }
    });
